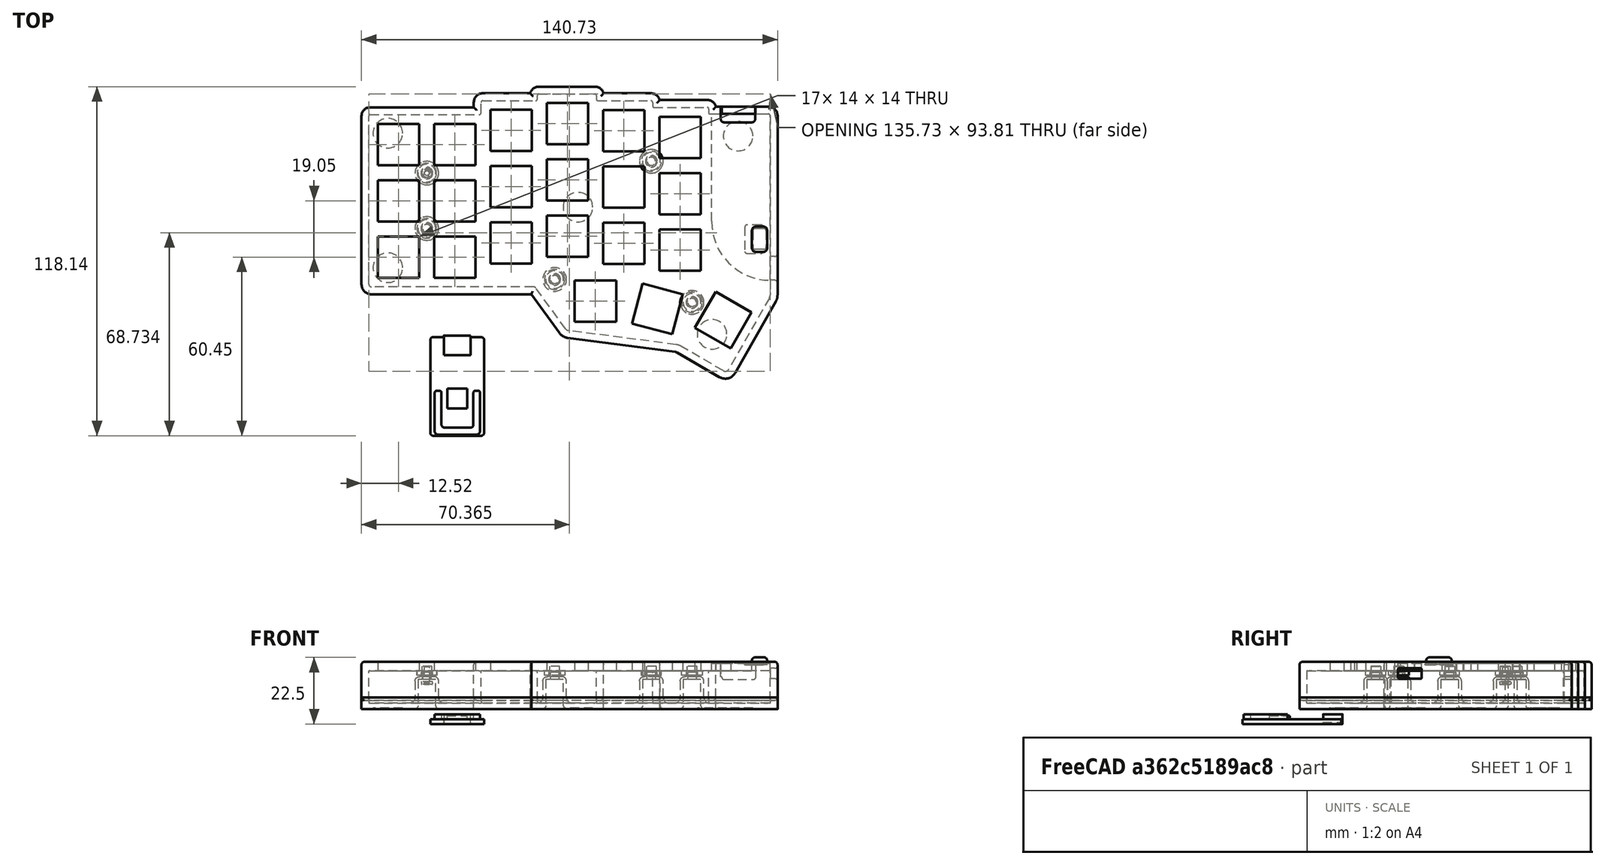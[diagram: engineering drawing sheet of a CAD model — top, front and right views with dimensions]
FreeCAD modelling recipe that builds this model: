
FCSTD DOCUMENT  (FreeCAD 1.0R39109 (Git))
Label: CaseV2
License: All rights reserved
LicenseURL: http://en.wikipedia.org/wiki/All_rights_reserved
objects: Sketcher::SketchObject×29, PartDesign::Pocket×15, PartDesign::Pad×13, PartDesign::Fillet×9, PartDesign::Body×5, Spreadsheet::Sheet×2
note: 174 computed .brp shape members not serialized (recipe doc carries the construction recipe); baked Part::Feature solids carry a one-line shape summary decoded from their .brp

FEATURE [Spreadsheet::Sheet] Spreadsheet
  cells = A1='PCBInnerBorderSpacing; B1(PCBInnerBorderSpacing)=1; A2='CaseTopBorderWitdh; B2(CaseTopBorderWitdh)=2; A3='SwitchBorderSpacing; B3(SwitchBorderSpacing)=2; A4='PCBBorderRadius; B4(PCBBorderRadius)=0.632; A5='PCBSmallStep; B5(PCBSmallStep)=2.25; A6='PCBBigStep; B6(PCBBigStep)=4.75; A7='SwitchplateHeight; B7(SwitchplateHeight)=2; A8='CaseTopTopBorderHeight; B8(CaseTopTopBorderHeight)=7; A9='CaseTopBottomBorderHeight; B9(CaseTopBottomBorderHeight)=6; A10='CaseColumnDiameter; B10(CaseColumnDiameter)=5; A11='ThreadedInsertHeight; B11(ThreadedInsertHeight)=3; A12='ThreadedInsertExtDiameter; B12(ThreadedInsertExtDiameter)=3.9; A13='PCBHoleSize; B13(PCBHoleSize)=4.2; A14='USBCPocketWidth; B14(USBCPocketWidth)=13.2; A15='USBCPocketHEIGHT; B15(USBCPocketHeight)=7.4; A16='CaseBottomPartHeight; B16(CaseBottomPartHeight)==CaseBottomFloorHeight + CaseBottomBorder; A17='CaseBottomFloorHeight; B17(CaseBottomFloorHeight)=3; A18='CaseBottomBorder; B18(CaseBottomBorder)=10; A19='ShadowLineWidth; B19(ShadowLineWidth)==CaseTopBorderWitdh - ShadowLineLipWidth; A20='ShadowLineLipWidth; B20(ShadowLineLipWidth)=0.6; A21='ResetSwitchHeight; B21(ResetSwitchHeight)=2.6; A22='PowerSwitchHeight; B22(PowerSwitchHeight)==3 - 1.4
FEATURE [Sketcher::SketchObject] Sketch108
  ArcFitTolerance = 0
  FullyConstrained = false
  MakeInternals = false
  Placement = pos=(0,0,8) rot=(0,0,1;0rad)
  sketch-geometry (26):
    g0: LineSegment StartX=-0.575516 StartY=59.75 StartZ=0 EndX=34.48 EndY=59.75 EndZ=0
    g1: LineSegment StartX=34.48 StartY=59.75 StartZ=0 EndX=34.48 EndY=61.4175 EndZ=0
    g2: ArcOfCircle CenterX=37.5625 CenterY=61.4175 CenterZ=0 NormalX=0 NormalY=0 NormalZ=1 AngleXU=0 Radius=3.08246 StartAngle=1.5708 EndAngle=3.14159
    g3: LineSegment StartX=37.5625 StartY=64.5 StartZ=0 EndX=53.5746 EndY=64.5 EndZ=0
    g4: ArcOfCircle CenterX=56.4769 CenterY=63.7531 CenterZ=0 NormalX=0 NormalY=0 NormalZ=1 AngleXU=0 Radius=2.99694 StartAngle=1.5708 EndAngle=2.8897
    g5: LineSegment StartX=56.4769 StartY=66.75 StartZ=0 EndX=75.4511 EndY=66.75 EndZ=0
    g6: ArcOfCircle CenterX=75.4511 CenterY=63.7211 CenterZ=0 NormalX=0 NormalY=0 NormalZ=1 AngleXU=0 Radius=3.0289 StartAngle=0.260077 EndAngle=1.5708
    g7: LineSegment StartX=78.3781 StartY=64.5 StartZ=0 EndX=94.3924 EndY=64.5 EndZ=0
    g8: ArcOfCircle CenterX=94.3924 CenterY=61.4124 CenterZ=0 NormalX=0 NormalY=0 NormalZ=1 AngleXU=0 Radius=3.08765 StartAngle=0.274732 EndAngle=1.5708
    g9: LineSegment StartX=97.3642 StartY=62.25 StartZ=0 EndX=113.447 EndY=62.25 EndZ=0
    g10: ArcOfCircle CenterX=113.447 CenterY=59.2166 CenterZ=0 NormalX=0 NormalY=0 NormalZ=1 AngleXU=0 Radius=3.03342 StartAngle=0.261223 EndAngle=1.5708
    g11: LineSegment StartX=116.377 StartY=60 StartZ=0 EndX=134.174 EndY=60 EndZ=0
    g12: ArcOfCircle CenterX=134.174 CenterY=56.9441 CenterZ=0 NormalX=0 NormalY=0 NormalZ=1 AngleXU=0 Radius=3.05595 StartAngle=0 EndAngle=1.5708
    g13: LineSegment StartX=137.23 StartY=56.9441 StartZ=0 EndX=137.23 EndY=-3.79962 EndZ=0
    g14: ArcOfCircle CenterX=132.762 CenterY=-3.79962 CenterZ=0 NormalX=0 NormalY=0 NormalZ=1 AngleXU=0 Radius=4.46789 StartAngle=5.76566 EndAngle=6.28319
    g15: LineSegment StartX=136.645 StartY=-6.01003 StartZ=0 EndX=122.927 EndY=-30.1062 EndZ=0
    g16: ArcOfCircle CenterX=119.558 CenterY=-28.1883 CenterZ=0 NormalX=0 NormalY=0 NormalZ=1 AngleXU=0 Radius=3.87659 StartAngle=4.18792 EndAngle=5.76566
    g17: LineSegment StartX=117.617 StartY=-31.5438 StartZ=0 EndX=103.226 EndY=-23.2181 EndZ=0
    g18: ArcOfCircle CenterX=102.379 CenterY=-24.6817 CenterZ=0 NormalX=0 NormalY=0 NormalZ=1 AngleXU=0 Radius=1.69085 StartAngle=1.04632 EndAngle=1.44147
    g19: LineSegment StartX=102.597 StartY=-23.0049 StartZ=0 EndX=66.2389 EndY=-18.2764 EndZ=0
    g20: ArcOfCircle CenterX=66.7544 CenterY=-14.3127 CenterZ=0 NormalX=0 NormalY=0 NormalZ=1 AngleXU=0 Radius=3.99704 StartAngle=3.77183 EndAngle=4.58306
    g21: LineSegment StartX=63.5253 StartY=-16.6683 StartZ=0 EndX=53.9192 EndY=-3.5 EndZ=0
    g22: LineSegment StartX=53.9192 StartY=-3.5 StartZ=0 EndX=-0.150389 EndY=-3.5 EndZ=0
    g23: ArcOfCircle CenterX=-0.150389 CenterY=-0.150389 CenterZ=0 NormalX=0 NormalY=0 NormalZ=1 AngleXU=0 Radius=3.34961 StartAngle=3.14159 EndAngle=4.71239
    g24: LineSegment StartX=-3.5 StartY=-0.150389 StartZ=0 EndX=-3.5 EndY=56.8255 EndZ=0
    g25: ArcOfCircle CenterX=-0.575516 CenterY=56.8255 CenterZ=0 NormalX=0 NormalY=0 NormalZ=1 AngleXU=0 Radius=2.92448 StartAngle=1.5708 EndAngle=3.14159
  constraints (36):
    c: Horizontal(g0)
    c: Coincident(g0,g1)
    c: Vertical(g1)
    c: Coincident(g1,g2)
    c: Coincident(g2,g3)
    c: Horizontal(g3)
    c: Coincident(g3,g4)
    c: Coincident(g4,g5)
    c: Horizontal(g5)
    c: Coincident(g5,g6)
    c: Coincident(g6,g7)
    c: Horizontal(g7)
    c: Coincident(g7,g8)
    c: Coincident(g8,g9)
    c: Horizontal(g9)
    c: Coincident(g9,g10)
    c: Coincident(g10,g11)
    c: Horizontal(g11)
    c: Coincident(g11,g12)
    c: Coincident(g12,g13)
    c: Vertical(g13)
    c: Coincident(g13,g14)
    c: Coincident(g14,g15)
    c: Coincident(g15,g16)
    c: Coincident(g16,g17)
    c: Coincident(g17,g18)
    c: Coincident(g18,g19)
    c: Coincident(g19,g20)
    c: Coincident(g20,g21)
    c: Coincident(g21,g22)
    c: Horizontal(g22)
    c: Coincident(g22,g23)
    c: Coincident(g23,g24)
    c: Vertical(g24)
    c: Coincident(g24,g25)
    c: Coincident(g25,g0)
FEATURE [PartDesign::Pad] Pad
  Direction = (0,0,1)
  Length = 4
  Length2 = 10
  Placement = pos=(0,0,8) rot=(0,0,1;0rad)
  Profile = -> Sketch108
  ReferenceAxis = -> Sketch108 [N_Axis]
  Suppressed = false
  Type = 0
FEATURE [Sketcher::SketchObject] Sketch110
  ArcFitTolerance = 0
  FullyConstrained = false
  MakeInternals = false
  Placement = pos=(0,0,8) rot=(0,0,1;0rad)
  sketch-geometry (26):
    g0: LineSegment StartX=-0.575516 StartY=59.75 StartZ=0 EndX=34.48 EndY=59.75 EndZ=0
    g1: LineSegment StartX=34.48 StartY=59.75 StartZ=0 EndX=34.48 EndY=61.4175 EndZ=0
    g2: ArcOfCircle CenterX=37.5625 CenterY=61.4175 CenterZ=0 NormalX=0 NormalY=0 NormalZ=1 AngleXU=0 Radius=3.08246 StartAngle=1.5708 EndAngle=3.14159
    g3: LineSegment StartX=37.5625 StartY=64.5 StartZ=0 EndX=53.5746 EndY=64.5 EndZ=0
    g4: ArcOfCircle CenterX=56.4769 CenterY=63.7531 CenterZ=0 NormalX=0 NormalY=0 NormalZ=1 AngleXU=0 Radius=2.99694 StartAngle=1.5708 EndAngle=2.8897
    g5: LineSegment StartX=56.4769 StartY=66.75 StartZ=0 EndX=75.4511 EndY=66.75 EndZ=0
    g6: ArcOfCircle CenterX=75.4511 CenterY=63.7211 CenterZ=0 NormalX=0 NormalY=0 NormalZ=1 AngleXU=0 Radius=3.0289 StartAngle=0.260077 EndAngle=1.5708
    g7: LineSegment StartX=78.3781 StartY=64.5 StartZ=0 EndX=94.3924 EndY=64.5 EndZ=0
    g8: ArcOfCircle CenterX=94.3924 CenterY=61.4124 CenterZ=0 NormalX=0 NormalY=0 NormalZ=1 AngleXU=0 Radius=3.08765 StartAngle=0.274732 EndAngle=1.5708
    g9: LineSegment StartX=97.3642 StartY=62.25 StartZ=0 EndX=113.447 EndY=62.25 EndZ=0
    g10: ArcOfCircle CenterX=113.447 CenterY=59.2166 CenterZ=0 NormalX=0 NormalY=0 NormalZ=1 AngleXU=0 Radius=3.03342 StartAngle=0.261223 EndAngle=1.5708
    g11: LineSegment StartX=116.377 StartY=60 StartZ=0 EndX=134.174 EndY=60 EndZ=0
    g12: ArcOfCircle CenterX=134.174 CenterY=56.9441 CenterZ=0 NormalX=0 NormalY=0 NormalZ=1 AngleXU=0 Radius=3.05595 StartAngle=0 EndAngle=1.5708
    g13: LineSegment StartX=137.23 StartY=56.9441 StartZ=0 EndX=137.23 EndY=-3.79962 EndZ=0
    g14: ArcOfCircle CenterX=132.762 CenterY=-3.79962 CenterZ=0 NormalX=0 NormalY=0 NormalZ=1 AngleXU=0 Radius=4.46789 StartAngle=5.76566 EndAngle=6.28319
    g15: LineSegment StartX=136.645 StartY=-6.01003 StartZ=0 EndX=122.927 EndY=-30.1062 EndZ=0
    g16: ArcOfCircle CenterX=119.558 CenterY=-28.1883 CenterZ=0 NormalX=0 NormalY=0 NormalZ=1 AngleXU=0 Radius=3.87659 StartAngle=4.18792 EndAngle=5.76566
    g17: LineSegment StartX=117.617 StartY=-31.5438 StartZ=0 EndX=103.226 EndY=-23.2181 EndZ=0
    g18: ArcOfCircle CenterX=102.379 CenterY=-24.6817 CenterZ=0 NormalX=0 NormalY=0 NormalZ=1 AngleXU=0 Radius=1.69085 StartAngle=1.04632 EndAngle=1.44147
    g19: LineSegment StartX=102.597 StartY=-23.0049 StartZ=0 EndX=66.2389 EndY=-18.2764 EndZ=0
    g20: ArcOfCircle CenterX=66.7544 CenterY=-14.3127 CenterZ=0 NormalX=0 NormalY=0 NormalZ=1 AngleXU=0 Radius=3.99704 StartAngle=3.77183 EndAngle=4.58306
    g21: LineSegment StartX=63.5253 StartY=-16.6683 StartZ=0 EndX=53.9192 EndY=-3.5 EndZ=0
    g22: LineSegment StartX=53.9192 StartY=-3.5 StartZ=0 EndX=-0.150389 EndY=-3.5 EndZ=0
    g23: ArcOfCircle CenterX=-0.150389 CenterY=-0.150389 CenterZ=0 NormalX=0 NormalY=0 NormalZ=1 AngleXU=0 Radius=3.34961 StartAngle=3.14159 EndAngle=4.71239
    g24: LineSegment StartX=-3.5 StartY=-0.150389 StartZ=0 EndX=-3.5 EndY=56.8255 EndZ=0
    g25: ArcOfCircle CenterX=-0.575516 CenterY=56.8255 CenterZ=0 NormalX=0 NormalY=0 NormalZ=1 AngleXU=0 Radius=2.92448 StartAngle=1.5708 EndAngle=3.14159
  constraints (36):
    c: Horizontal(g0)
    c: Coincident(g0,g1)
    c: Vertical(g1)
    c: Coincident(g1,g2)
    c: Coincident(g2,g3)
    c: Horizontal(g3)
    c: Coincident(g3,g4)
    c: Coincident(g4,g5)
    c: Horizontal(g5)
    c: Coincident(g5,g6)
    c: Coincident(g6,g7)
    c: Horizontal(g7)
    c: Coincident(g7,g8)
    c: Coincident(g8,g9)
    c: Horizontal(g9)
    c: Coincident(g9,g10)
    c: Coincident(g10,g11)
    c: Horizontal(g11)
    c: Coincident(g11,g12)
    c: Coincident(g12,g13)
    c: Vertical(g13)
    c: Coincident(g13,g14)
    c: Coincident(g14,g15)
    c: Coincident(g15,g16)
    c: Coincident(g16,g17)
    c: Coincident(g17,g18)
    c: Coincident(g18,g19)
    c: Coincident(g19,g20)
    c: Coincident(g20,g21)
    c: Coincident(g21,g22)
    c: Horizontal(g22)
    c: Coincident(g22,g23)
    c: Coincident(g23,g24)
    c: Vertical(g24)
    c: Coincident(g24,g25)
    c: Coincident(g25,g0)
FEATURE [PartDesign::Pad] Pad028  label="Main Shape"
  Direction = (0,0,1)
  Length = 13
  Length2 = 10
  Placement = pos=(0,0,8) rot=(0,0,1;0rad)
  Profile = -> Sketch110
  ReferenceAxis = -> Sketch110 [N_Axis]
  Suppressed = false
  Type = 0
FEATURE [Sketcher::SketchObject] Sketch109  label="Case.TopBorder001"
  ArcFitTolerance = 0
  AttachmentOffset = pos=(0,0,-13) rot=(0,0,1;0rad)
  AttachmentSupport = -> [Pad028]
  FullyConstrained = false
  MakeInternals = false
  MapMode = 5
  Placement = pos=(0,0,8) rot=(0,0,1;0rad)
  sketch-geometry (36):
    g0: LineSegment StartX=-0.575516 StartY=57.25 StartZ=0 EndX=36.2169 EndY=57.25 EndZ=0
    g1: LineSegment StartX=36.98 StartY=58.0131 StartZ=0 EndX=36.98 EndY=61.4175 EndZ=0
    g2: LineSegment StartX=37.5625 StartY=62 StartZ=0 EndX=55.4164 EndY=62 EndZ=0
    g3: LineSegment StartX=55.98 StartY=62.5636 StartZ=0 EndX=55.98 EndY=63.7531 EndZ=0
    g4: LineSegment StartX=56.4769 StartY=64.25 StartZ=0 EndX=75.4511 EndY=64.25 EndZ=0
    g5: LineSegment StartX=75.98 StartY=63.7211 StartZ=0 EndX=75.98 EndY=62.4917 EndZ=0
    g6: LineSegment StartX=76.4717 StartY=62 StartZ=0 EndX=94.3924 EndY=62 EndZ=0
    g7: LineSegment StartX=94.98 StartY=61.4124 StartZ=0 EndX=94.98 EndY=60.1933 EndZ=0
    g8: LineSegment StartX=95.4233 StartY=59.75 StartZ=0 EndX=113.447 EndY=59.75 EndZ=0
    g9: LineSegment StartX=113.98 StartY=59.2166 StartZ=0 EndX=113.98 EndY=57.754 EndZ=0
    g10: LineSegment StartX=114.234 StartY=57.5 StartZ=0 EndX=134.174 EndY=57.5 EndZ=0
    g11: LineSegment StartX=134.73 StartY=56.9441 StartZ=0 EndX=134.73 EndY=-3.79962 EndZ=0
    g12: LineSegment StartX=134.472 StartY=-4.7732 StartZ=0 EndX=120.755 EndY=-28.8693 EndZ=0
    g13: LineSegment StartX=118.869 StartY=-29.3799 StartZ=0 EndX=104.478 EndY=-21.0541 EndZ=0
    g14: LineSegment StartX=102.919 StartY=-20.5258 StartZ=0 EndX=66.5613 EndY=-15.7973 EndZ=0
    g15: LineSegment StartX=65.545 StartY=-15.195 StartZ=0 EndX=55.5069 EndY=-1.43443 EndZ=0
    g16: LineSegment StartX=54.6523 StartY=-1 StartZ=0 EndX=-0.150389 EndY=-1 EndZ=0
    g17: LineSegment StartX=-1 StartY=-0.150389 StartZ=0 EndX=-1 EndY=56.8255 EndZ=0
    g18: ArcOfCircle CenterX=37.5625 CenterY=61.4175 CenterZ=0 NormalX=0 NormalY=0 NormalZ=1 AngleXU=0 Radius=0.582459 StartAngle=1.5708 EndAngle=3.14159
    g19: ArcOfCircle CenterX=55.4164 CenterY=62.5636 CenterZ=0 NormalX=0 NormalY=0 NormalZ=1 AngleXU=0 Radius=0.563591 StartAngle=4.71239 EndAngle=6.28319
    g20: ArcOfCircle CenterX=56.4769 CenterY=63.7531 CenterZ=0 NormalX=0 NormalY=0 NormalZ=1 AngleXU=0 Radius=0.496936 StartAngle=1.5708 EndAngle=3.14159
    g21: ArcOfCircle CenterX=75.4511 CenterY=63.7211 CenterZ=0 NormalX=0 NormalY=0 NormalZ=1 AngleXU=0 Radius=0.528895 StartAngle=0 EndAngle=1.5708
    g22: ArcOfCircle CenterX=76.4717 CenterY=62.4917 CenterZ=0 NormalX=0 NormalY=0 NormalZ=1 AngleXU=0 Radius=0.491748 StartAngle=3.14159 EndAngle=4.71239
    g23: ArcOfCircle CenterX=94.3924 CenterY=61.4124 CenterZ=0 NormalX=0 NormalY=0 NormalZ=1 AngleXU=0 Radius=0.587645 StartAngle=0 EndAngle=1.5708
    g24: ArcOfCircle CenterX=95.4233 CenterY=60.1933 CenterZ=0 NormalX=0 NormalY=0 NormalZ=1 AngleXU=0 Radius=0.443253 StartAngle=3.14159 EndAngle=4.71239
    g25: ArcOfCircle CenterX=113.447 CenterY=59.2166 CenterZ=0 NormalX=0 NormalY=0 NormalZ=1 AngleXU=0 Radius=0.533416 StartAngle=0 EndAngle=1.5708
    g26: ArcOfCircle CenterX=134.174 CenterY=56.9441 CenterZ=0 NormalX=0 NormalY=0 NormalZ=1 AngleXU=0 Radius=0.555946 StartAngle=0 EndAngle=1.5708
    g27: ArcOfCircle CenterX=119.558 CenterY=-28.1883 CenterZ=0 NormalX=0 NormalY=0 NormalZ=1 AngleXU=0 Radius=1.37659 StartAngle=4.18792 EndAngle=5.76566
    g28: ArcOfCircle CenterX=-0.150389 CenterY=-0.150389 CenterZ=0 NormalX=0 NormalY=0 NormalZ=1 AngleXU=0 Radius=0.849611 StartAngle=3.14159 EndAngle=4.71239
    g29: ArcOfCircle CenterX=36.2169 CenterY=58.0131 CenterZ=0 NormalX=0 NormalY=0 NormalZ=1 AngleXU=0 Radius=0.763133 StartAngle=4.71239 EndAngle=6.28319
    g30: ArcOfCircle CenterX=114.234 CenterY=57.754 CenterZ=0 NormalX=0 NormalY=0 NormalZ=1 AngleXU=0 Radius=0.253983 StartAngle=3.14159 EndAngle=4.71239
    g31: ArcOfCircle CenterX=-0.575516 CenterY=56.8255 CenterZ=0 NormalX=0 NormalY=0 NormalZ=1 AngleXU=0 Radius=0.424484 StartAngle=1.5708 EndAngle=3.14159
    g32: ArcOfCircle CenterX=54.6523 CenterY=-2.05788 CenterZ=0 NormalX=0 NormalY=0 NormalZ=1 AngleXU=0 Radius=1.05788 StartAngle=0.630238 EndAngle=1.5708
    g33: ArcOfCircle CenterX=66.7544 CenterY=-14.3127 CenterZ=0 NormalX=0 NormalY=0 NormalZ=1 AngleXU=0 Radius=1.49704 StartAngle=3.77183 EndAngle=4.58306
    g34: ArcOfCircle CenterX=102.379 CenterY=-24.6817 CenterZ=0 NormalX=0 NormalY=0 NormalZ=1 AngleXU=0 Radius=4.19085 StartAngle=1.04632 EndAngle=1.44147
    g35: ArcOfCircle CenterX=132.762 CenterY=-3.79962 CenterZ=0 NormalX=0 NormalY=0 NormalZ=1 AngleXU=0 Radius=1.96789 StartAngle=5.76566 EndAngle=6.28319
  constraints (36):
    c: Coincident(g17,g28)
    c: Coincident(g16,g28)
    c: Coincident(g0,g29)
    c: Coincident(g1,g29)
    c: Coincident(g1,g18)
    c: Coincident(g2,g18)
    c: Coincident(g2,g19)
    c: Coincident(g3,g19)
    c: Coincident(g3,g20)
    c: Coincident(g4,g20)
    c: Coincident(g4,g21)
    c: Coincident(g5,g22)
    c: Coincident(g5,g21)
    c: Coincident(g6,g22)
    c: Coincident(g6,g23)
    c: Coincident(g7,g24)
    c: Coincident(g7,g23)
    c: Coincident(g8,g24)
    c: Coincident(g8,g25)
    c: Coincident(g9,g25)
    c: Coincident(g13,g27)
    c: Coincident(g12,g27)
    c: Coincident(g10,g26)
    c: Coincident(g11,g26)
    c: Tangent(g9,g30) = -1.5708
    c: Tangent(g10,g30) = -1.5708
    c: Tangent(g0,g31) = 1.5708
    c: Tangent(g17,g31) = 1.5708
    c: Tangent(g16,g32) = -1.5708
    c: Tangent(g15,g32) = -1.5708
    c: Tangent(g15,g33) = 1.5708
    c: Tangent(g14,g33) = 1.5708
    c: Tangent(g14,g34) = -1.5708
    c: Tangent(g13,g34) = -1.5708
    c: Tangent(g11,g35) = 1.5708
    c: Tangent(g12,g35) = 1.5708
FEATURE [PartDesign::Pocket] Pocket021  label="Border"
  BaseFeature = -> Pad028
  Direction = (0,0,-1)
  Length = 10
  Length2 = 5
  Placement = pos=(0,0,8) rot=(0,0,1;0rad)
  Profile = -> Sketch109
  ReferenceAxis = -> Sketch109 [N_Axis]
  Reversed = true
  Suppressed = false
  Type = 0
FEATURE [PartDesign::Fillet] Fillet003  label="Top Border Radius"
  Base = -> Pocket021 [Edge90,Edge91,Edge92,Edge89,Edge88,Edge87,Edge86,Edge85,Edge84,Edge83,Edge82,Edge81,Edge80,Edge79,Edge78,Edge77,Edge76,Edge75,Edge74,Edge73,Edge72,Edge71,Edge70,Edge10,Edge4,Edge7]
  BaseFeature = -> Pocket021
  Placement = pos=(0,0,8) rot=(0,0,1;0rad)
  Radius = 1
  SupportTransform = false
  Suppressed = false
  UseAllEdges = false
FEATURE [Sketcher::SketchObject] Sketch111  label="Case.SwitchPlatePocket001"
  ArcFitTolerance = 0
  AttachmentSupport = -> [Fillet003]
  FullyConstrained = false
  MakeInternals = false
  MapMode = 5
  Placement = pos=(0,0,21) rot=(0,0,1;0rad)
  expr: .Placement.Base.z = Spreadsheet001.CaseTopBottomBorderHeight + Spreadsheet001.SwitchplateHeight
  sketch-geometry (115):
    g0: LineSegment StartX=68.62 StartY=1.21 StartZ=0 EndX=82.62 EndY=1.21 EndZ=0
    g1: LineSegment StartX=82.62 StartY=1.21 StartZ=0 EndX=82.62 EndY=-12.79 EndZ=0
    g2: LineSegment StartX=82.62 StartY=-12.79 StartZ=0 EndX=68.62 EndY=-12.79 EndZ=0
    g3: LineSegment StartX=68.62 StartY=-12.79 StartZ=0 EndX=68.62 EndY=1.21 EndZ=0
    g4: LineSegment StartX=91.6293 StartY=0.0893034 StartZ=0 EndX=105.156 EndY=-3.52 EndZ=0
    g5: LineSegment StartX=105.156 StartY=-3.52 StartZ=0 EndX=101.547 EndY=-17.0467 EndZ=0
    g6: LineSegment StartX=101.547 StartY=-17.0467 StartZ=0 EndX=88.02 EndY=-13.4374 EndZ=0
    g7: LineSegment StartX=88.02 StartY=-13.4374 StartZ=0 EndX=91.6293 EndY=0.0893034 EndZ=0
    g8: LineSegment StartX=116.275 StartY=-2.66 StartZ=0 EndX=128.399 EndY=-9.66 EndZ=0
    g9: LineSegment StartX=128.399 StartY=-9.66 StartZ=0 EndX=121.399 EndY=-21.7844 EndZ=0
    g10: LineSegment StartX=121.399 StartY=-21.7844 StartZ=0 EndX=109.277 EndY=-14.7856 EndZ=0
    g11: LineSegment StartX=109.277 StartY=-14.7856 StartZ=0 EndX=116.275 EndY=-2.66 EndZ=0
    g12: Circle [constr] CenterX=108.346 CenterY=-6.24282 CenterZ=0 NormalX=0 NormalY=0 NormalZ=1 AngleXU=0 Radius=1.14051
    g13: Circle [constr] CenterX=61.8361 CenterY=1.51 CenterZ=0 NormalX=0 NormalY=0 NormalZ=1 AngleXU=0 Radius=1.14411
    g14: Circle [constr] CenterX=18.6 CenterY=18.76 CenterZ=0 NormalX=0 NormalY=0 NormalZ=1 AngleXU=0 Radius=1.14013
    g15: Circle [constr] CenterX=18.6 CenterY=37.51 CenterZ=0 NormalX=0 NormalY=0 NormalZ=1 AngleXU=0 Radius=1.14152
    g16: Circle [constr] CenterX=94.6 CenterY=41.2626 CenterZ=0 NormalX=0 NormalY=0 NormalZ=1 AngleXU=0 Radius=1.14274
    g17: LineSegment StartX=2.02 StartY=54.16 StartZ=0 EndX=2.02 EndY=40.16 EndZ=0
    g18: LineSegment StartX=2.02 StartY=2.06 StartZ=0 EndX=16.02 EndY=2.06 EndZ=0
    g19: LineSegment StartX=35.07 StartY=54.16 StartZ=0 EndX=21.07 EndY=54.16 EndZ=0
    g20: LineSegment StartX=35.07 StartY=40.16 StartZ=0 EndX=21.07 EndY=40.16 EndZ=0
    g21: LineSegment StartX=35.07 StartY=16.06 StartZ=0 EndX=21.07 EndY=16.06 EndZ=0
    g22: LineSegment StartX=2.02 StartY=35.11 StartZ=0 EndX=16.02 EndY=35.11 EndZ=0
    g23: LineSegment StartX=2.02 StartY=21.11 StartZ=0 EndX=16.02 EndY=21.11 EndZ=0
    g24: LineSegment StartX=16.02 StartY=54.16 StartZ=0 EndX=16.02 EndY=40.16 EndZ=0
    g25: LineSegment StartX=21.07 StartY=2.06 StartZ=0 EndX=21.07 EndY=16.06 EndZ=0
    g26: LineSegment StartX=35.07 StartY=54.16 StartZ=0 EndX=35.07 EndY=40.16 EndZ=0
    g27: LineSegment StartX=40.12 StartY=58.97 StartZ=0 EndX=40.12 EndY=44.97 EndZ=0
    g28: LineSegment StartX=54.12 StartY=6.87 StartZ=0 EndX=54.12 EndY=20.87 EndZ=0
    g29: LineSegment StartX=59.17 StartY=61.27 StartZ=0 EndX=59.17 EndY=47.27 EndZ=0
    g30: LineSegment StartX=73.17 StartY=9.17 StartZ=0 EndX=73.17 EndY=23.17 EndZ=0
    g31: LineSegment StartX=78.22 StartY=58.87 StartZ=0 EndX=78.22 EndY=44.87 EndZ=0
    g32: LineSegment StartX=92.22 StartY=6.77 StartZ=0 EndX=92.22 EndY=20.77 EndZ=0
    g33: LineSegment StartX=97.27 StartY=56.54 StartZ=0 EndX=97.27 EndY=42.54 EndZ=0
    g34: LineSegment StartX=111.27 StartY=56.54 StartZ=0 EndX=111.27 EndY=42.54 EndZ=0
    g35: LineSegment StartX=40.12 StartY=44.97 StartZ=0 EndX=54.12 EndY=44.97 EndZ=0
    g36: LineSegment StartX=40.12 StartY=39.92 StartZ=0 EndX=54.12 EndY=39.92 EndZ=0
    g37: LineSegment StartX=40.12 StartY=6.87 StartZ=0 EndX=54.12 EndY=6.87 EndZ=0
    g38: LineSegment StartX=59.17 StartY=9.17 StartZ=0 EndX=73.17 EndY=9.17 EndZ=0
    g39: LineSegment StartX=59.17 StartY=23.17 StartZ=0 EndX=73.17 EndY=23.17 EndZ=0
    g40: LineSegment StartX=59.17 StartY=28.22 StartZ=0 EndX=73.17 EndY=28.22 EndZ=0
    g41: LineSegment StartX=59.17 StartY=42.22 StartZ=0 EndX=73.17 EndY=42.22 EndZ=0
    g42: LineSegment StartX=59.17 StartY=47.27 StartZ=0 EndX=73.17 EndY=47.27 EndZ=0
    g43: LineSegment StartX=16.02 StartY=54.16 StartZ=0 EndX=2.02 EndY=54.16 EndZ=0
    g44: LineSegment StartX=16.02 StartY=40.16 StartZ=0 EndX=2.02 EndY=40.16 EndZ=0
    g45: LineSegment StartX=21.07 StartY=21.11 StartZ=0 EndX=35.07 EndY=21.11 EndZ=0
    g46: LineSegment StartX=16.02 StartY=16.06 StartZ=0 EndX=2.02 EndY=16.06 EndZ=0
    g47: LineSegment StartX=16.02 StartY=16.06 StartZ=0 EndX=16.02 EndY=2.06 EndZ=0
    g48: LineSegment StartX=21.07 StartY=21.11 StartZ=0 EndX=21.07 EndY=35.11 EndZ=0
    g49: LineSegment StartX=21.07 StartY=40.16 StartZ=0 EndX=21.07 EndY=54.16 EndZ=0
    g50: LineSegment StartX=16.02 StartY=35.11 StartZ=0 EndX=16.02 EndY=21.11 EndZ=0
    g51: LineSegment StartX=35.07 StartY=35.11 StartZ=0 EndX=35.07 EndY=21.11 EndZ=0
    g52: LineSegment StartX=35.07 StartY=16.06 StartZ=0 EndX=35.07 EndY=2.06 EndZ=0
    g53: LineSegment StartX=54.12 StartY=44.97 StartZ=0 EndX=54.12 EndY=58.97 EndZ=0
    g54: LineSegment StartX=54.12 StartY=25.92 StartZ=0 EndX=54.12 EndY=39.92 EndZ=0
    g55: LineSegment StartX=97.27 StartY=42.54 StartZ=0 EndX=111.27 EndY=42.54 EndZ=0
    g56: LineSegment StartX=97.27 StartY=37.49 StartZ=0 EndX=111.27 EndY=37.49 EndZ=0
    g57: LineSegment StartX=97.27 StartY=23.49 StartZ=0 EndX=111.27 EndY=23.49 EndZ=0
    g58: LineSegment StartX=97.27 StartY=18.44 StartZ=0 EndX=111.27 EndY=18.44 EndZ=0
    g59: LineSegment StartX=97.27 StartY=4.44 StartZ=0 EndX=111.27 EndY=4.44 EndZ=0
    g60: LineSegment StartX=73.17 StartY=28.22 StartZ=0 EndX=73.17 EndY=42.22 EndZ=0
    g61: LineSegment StartX=78.22 StartY=44.87 StartZ=0 EndX=92.22 EndY=44.87 EndZ=0
    g62: LineSegment StartX=73.17 StartY=47.27 StartZ=0 EndX=73.17 EndY=61.27 EndZ=0
    g63: LineSegment StartX=92.22 StartY=25.82 StartZ=0 EndX=92.22 EndY=39.82 EndZ=0
    g64: LineSegment StartX=78.22 StartY=6.77 StartZ=0 EndX=92.22 EndY=6.77 EndZ=0
    g65: LineSegment StartX=78.22 StartY=20.77 StartZ=0 EndX=92.22 EndY=20.77 EndZ=0
    g66: LineSegment StartX=78.22 StartY=25.82 StartZ=0 EndX=92.22 EndY=25.82 EndZ=0
    g67: LineSegment StartX=78.22 StartY=20.77 StartZ=0 EndX=78.22 EndY=6.77 EndZ=0
    g68: LineSegment StartX=78.22 StartY=39.82 StartZ=0 EndX=92.22 EndY=39.82 EndZ=0
    g69: LineSegment StartX=59.17 StartY=42.22 StartZ=0 EndX=59.17 EndY=28.22 EndZ=0
    g70: LineSegment StartX=78.22 StartY=39.82 StartZ=0 EndX=78.22 EndY=25.82 EndZ=0
    g71: LineSegment StartX=92.22 StartY=44.87 StartZ=0 EndX=92.22 EndY=58.87 EndZ=0
    g72: LineSegment StartX=40.12 StartY=39.92 StartZ=0 EndX=40.12 EndY=25.92 EndZ=0
    g73: LineSegment StartX=40.12 StartY=20.87 StartZ=0 EndX=40.12 EndY=6.87 EndZ=0
    g74: LineSegment StartX=97.27 StartY=18.44 StartZ=0 EndX=97.27 EndY=4.44 EndZ=0
    g75: LineSegment StartX=111.27 StartY=18.44 StartZ=0 EndX=111.27 EndY=4.44 EndZ=0
    g76: LineSegment StartX=111.27 StartY=37.49 StartZ=0 EndX=111.27 EndY=23.49 EndZ=0
    g77: LineSegment StartX=97.27 StartY=37.49 StartZ=0 EndX=97.27 EndY=23.49 EndZ=0
    g78: LineSegment StartX=78.22 StartY=58.87 StartZ=0 EndX=92.22 EndY=58.87 EndZ=0
    g79: LineSegment StartX=59.17 StartY=23.17 StartZ=0 EndX=59.17 EndY=9.17 EndZ=0
    g80: LineSegment StartX=2.02 StartY=35.11 StartZ=0 EndX=2.02 EndY=21.11 EndZ=0
    g81: LineSegment StartX=2.02 StartY=16.06 StartZ=0 EndX=2.02 EndY=2.06 EndZ=0
    g82: LineSegment StartX=111.27 StartY=56.54 StartZ=0 EndX=97.27 EndY=56.54 EndZ=0
    g83: LineSegment StartX=40.12 StartY=58.97 StartZ=0 EndX=54.12 EndY=58.97 EndZ=0
    g84: LineSegment StartX=40.12 StartY=20.87 StartZ=0 EndX=54.12 EndY=20.87 EndZ=0
    g85: LineSegment StartX=21.07 StartY=2.06 StartZ=0 EndX=35.07 EndY=2.06 EndZ=0
    g86: LineSegment StartX=40.12 StartY=25.92 StartZ=0 EndX=54.12 EndY=25.92 EndZ=0
    g87: LineSegment [constr] StartX=109.277 StartY=-14.7856 StartZ=0 EndX=109.277 EndY=-18.8356 EndZ=0
    g88: LineSegment [constr] StartX=88.02 StartY=-13.4374 StartZ=0 EndX=88.02 EndY=-63.3371 EndZ=0
    g89: LineSegment [constr] StartX=101.547 StartY=-17.0467 StartZ=0 EndX=109.277 EndY=-17.0467 EndZ=0
    g90: LineSegment [constr] StartX=0.08 StartY=56.27 StartZ=0 EndX=0.08 EndY=0.01 EndZ=0
    g91: LineSegment [constr] StartX=0.08 StartY=56.27 StartZ=0 EndX=38.09 EndY=56.27 EndZ=0
    g92: LineSegment [constr] StartX=0.08 StartY=0.01 StartZ=0 EndX=55.8461 EndY=0.01 EndZ=0
    g93: LineSegment [constr] StartX=55.8461 StartY=0.01 StartZ=0 EndX=66.6118 EndY=-14.7264 EndZ=0
    g94: LineSegment [constr] StartX=66.6118 StartY=-14.7264 StartZ=0 EndX=104.029 EndY=-19.5728 EndZ=0
    g95: LineSegment [constr] StartX=104.029 StartY=-19.5728 StartZ=0 EndX=119.75 EndY=-28.6236 EndZ=0
    g96: LineSegment [constr] StartX=119.75 StartY=-28.6236 StartZ=0 EndX=133.476 EndY=-4.78248 EndZ=0
    g97: LineSegment [constr] StartX=113.11 StartY=58.5126 StartZ=0 EndX=113.11 EndY=6.94265 EndZ=0
    g98: LineSegment [constr] StartX=113.11 StartY=6.94265 StartZ=0 EndX=133.476 EndY=-4.78248 EndZ=0
    g99: LineSegment [constr] StartX=94.09 StartY=58.5126 StartZ=0 EndX=113.11 EndY=58.5126 EndZ=0
    g100: LineSegment [constr] StartX=94.09 StartY=61.0126 StartZ=0 EndX=94.09 EndY=58.5126 EndZ=0
    g101: LineSegment [constr] StartX=38.09 StartY=61.02 StartZ=0 EndX=57.08 EndY=61.02 EndZ=0
    g102: LineSegment [constr] StartX=57.08 StartY=63.26 StartZ=0 EndX=75.08 EndY=63.26 EndZ=0
    g103: LineSegment [constr] StartX=57.08 StartY=63.26 StartZ=0 EndX=57.08 EndY=61.02 EndZ=0
    g104: LineSegment [constr] StartX=75.08 StartY=61.02 StartZ=0 EndX=75.08 EndY=63.26 EndZ=0
    g105: LineSegment [constr] StartX=75.08 StartY=61.02 StartZ=0 EndX=94.09 EndY=61.0126 EndZ=0
    g106: LineSegment [constr] StartX=38.09 StartY=61.02 StartZ=0 EndX=38.09 EndY=56.27 EndZ=0
    g107: LineSegment StartX=73.17 StartY=61.27 StartZ=0 EndX=59.17 EndY=61.27 EndZ=0
    g108: LineSegment StartX=21.07 StartY=35.11 StartZ=0 EndX=35.07 EndY=35.11 EndZ=0
    g109: LineSegment [constr] StartX=114.544 StartY=22.1265 StartZ=0 EndX=114.544 EndY=57.5 EndZ=0
    g110: LineSegment [constr] StartX=115.521 StartY=21.15 StartZ=0 EndX=134.73 EndY=21.15 EndZ=0
    g111: LineSegment [constr] StartX=114.544 StartY=57.5 StartZ=0 EndX=134.174 EndY=57.5 EndZ=0
    g112: LineSegment [constr] StartX=134.73 StartY=21.15 StartZ=0 EndX=134.73 EndY=56.9444 EndZ=0
    g113: ArcOfCircle [constr] CenterX=134.174 CenterY=56.9444 CenterZ=0 NormalX=0 NormalY=0 NormalZ=1 AngleXU=0 Radius=0.555602 StartAngle=0 EndAngle=1.5708
    g114: ArcOfCircle [constr] CenterX=115.521 CenterY=22.1265 CenterZ=0 NormalX=0 NormalY=0 NormalZ=1 AngleXU=0 Radius=0.976478 StartAngle=3.14159 EndAngle=4.71239
  constraints (97):
    c: Coincident(g18,g81)
    c: Coincident(g46,g81)
    c: Coincident(g23,g80)
    c: Coincident(g22,g80)
    c: Coincident(g17,g44)
    c: Coincident(g17,g43)
    c: Coincident(g18,g47)
    c: Coincident(g46,g47)
    c: Coincident(g23,g50)
    c: Coincident(g22,g50)
    c: Coincident(g24,g44)
    c: Coincident(g24,g43)
    c: Coincident(g25,g85)
    c: Coincident(g21,g25)
    c: Coincident(g45,g48)
    c: Coincident(g48,g108)
    c: Coincident(g20,g49)
    c: Coincident(g19,g49)
    c: Coincident(g52,g85)
    c: Coincident(g21,g52)
    c: Coincident(g45,g51)
    c: Coincident(g51,g108)
    c: Coincident(g20,g26)
    c: Coincident(g19,g26)
    c: Coincident(g37,g73)
    c: Coincident(g73,g84)
    c: Coincident(g72,g86)
    c: Coincident(g36,g72)
    c: Coincident(g27,g35)
    c: Coincident(g27,g83)
    c: Coincident(g28,g37)
    c: Coincident(g28,g84)
    c: Coincident(g54,g86)
    c: Coincident(g36,g54)
    c: Coincident(g35,g53)
    c: Coincident(g53,g83)
    c: Coincident(g38,g79)
    c: Coincident(g39,g79)
    c: Coincident(g40,g69)
    c: Coincident(g41,g69)
    c: Coincident(g29,g42)
    c: Coincident(g29,g107)
    c: Coincident(g2,g3)
    c: Coincident(g0,g3)
    c: Coincident(g30,g38)
    c: Coincident(g30,g39)
    c: Coincident(g40,g60)
    c: Coincident(g41,g60)
    c: Coincident(g42,g62)
    c: Coincident(g62,g107)
    c: Coincident(g64,g67)
    c: Coincident(g65,g67)
    c: Coincident(g66,g70)
    c: Coincident(g68,g70)
    c: Coincident(g31,g61)
    c: Coincident(g31,g78)
    c: Coincident(g1,g2)
    c: Coincident(g0,g1)
    c: Coincident(g6,g7)
    c: Coincident(g4,g7)
    c: Coincident(g32,g64)
    c: Coincident(g32,g65)
    c: Coincident(g63,g66)
    c: Coincident(g63,g68)
    c: Coincident(g61,g71)
    c: Coincident(g71,g78)
    c: Coincident(g59,g74)
    c: Coincident(g58,g74)
    c: Coincident(g57,g77)
    c: Coincident(g56,g77)
    c: Coincident(g33,g55)
    c: Coincident(g33,g82)
    c: Coincident(g5,g6)
    c: Coincident(g4,g5)
    c: Coincident(g10,g11)
    c: Coincident(g59,g75)
    c: Coincident(g58,g75)
    c: Coincident(g57,g76)
    c: Coincident(g56,g76)
    c: Coincident(g34,g55)
    c: Coincident(g34,g82)
    c: Coincident(g8,g11)
    c: Coincident(g9,g10)
    c: Coincident(g8,g9)
    c: Vertical(g109)
    c: Horizontal(g110)
    c: Coincident(g111,g109)
    c: Horizontal(g111)
    c: Coincident(g112,g110)
    c: Vertical(g112)
    c: Tangent(g111,g113) = 1.5708
    c: Tangent(g112,g113) = -1.5708
    c: Tangent(g109,g114) = 1.5708
    c: Tangent(g110,g114) = -1.5708
    c: Equal(g49,g19)
    c: Equal(g19,g26)
    c: Equal(g26,g20)
FEATURE [Spreadsheet::Sheet] Spreadsheet001
  cells = A1='PCBInnerBorderSpacing; B1(PCBInnerBorderSpacing)=1; A2='CaseTopBorderWitdh; B2(CaseTopBorderWitdh)=2; A3='SwitchBorderSpacing; B3(SwitchBorderSpacing)=2; A4='PCBBorderRadius; B4(PCBBorderRadius)=0.632; A5='PCBSmallStep; B5(PCBSmallStep)=2.25; A6='PCBBigStep; B6(PCBBigStep)=4.75; A7='SwitchplateHeight; B7(SwitchplateHeight)=2; A8='CaseTopTopBorderHeight; B8(CaseTopTopBorderHeight)=7; A9='CaseTopBottomBorderHeight; B9(CaseTopBottomBorderHeight)=6; A10='CaseColumnDiameter; B10(CaseColumnDiameter)=5; A11='ThreadedInsertHeight; B11(ThreadedInsertHeight)=3; A12='ThreadedInsertExtDiameter; B12(ThreadedInsertExtDiameter)=3.9; A13='PCBHoleSize; B13(PCBHoleSize)=4.2; A14='USBCPocketWidth; B14(USBCPocketWidth)=13.2; A15='USBCPocketHEIGHT; B15(USBCPocketHeight)=7.4; A16='CaseBottomPartHeight; B16(CaseBottomPartHeight)==CaseBottomFloorHeight + CaseBottomBorder; A17='CaseBottomFloorHeight; B17(CaseBottomFloorHeight)=3; A18='CaseBottomBorder; B18(CaseBottomBorder)=10; A19='ShadowLineWidth; B19(ShadowLineWidth)==CaseTopBorderWitdh - ShadowLineLipWidth; A20='ShadowLineLipWidth; B20(ShadowLineLipWidth)=0.6; A21='ResetSwitchHeight; B21(ResetSwitchHeight)=2.6; A22='PowerSwitchHeight; B22(PowerSwitchHeight)==3 - 1.4
FEATURE [PartDesign::Pocket] Pocket022  label="Switch Plate"
  BaseFeature = -> Fillet003
  Direction = (0,0,-1)
  Length = 3
  Length2 = 5
  Placement = pos=(0,0,8) rot=(0,0,1;0rad)
  Profile = -> Sketch111
  ReferenceAxis = -> Sketch111 [N_Axis]
  Suppressed = false
  Type = 0
FEATURE [Sketcher::SketchObject] Sketch114
  ArcFitTolerance = 0
  AttachmentSupport = -> [Pocket022]
  FullyConstrained = false
  MakeInternals = false
  MapMode = 5
  Placement = pos=(137.23,0,8) rot=(0.57735,0.57735,0.57735;2.0944rad)
  sketch-geometry (10):
    g0: LineSegment StartX=1.24469 StartY=10.4386 StartZ=0 EndX=1.24469 EndY=7.69946 EndZ=0
    g1: LineSegment StartX=1.64469 StartY=10.8386 StartZ=0 EndX=8.89469 EndY=10.8386 EndZ=0
    g2: LineSegment StartX=1.64469 StartY=7.29946 StartZ=0 EndX=8.89469 EndY=7.29946 EndZ=0
    g3: LineSegment StartX=9.29469 StartY=10.4386 StartZ=0 EndX=9.29469 EndY=7.69946 EndZ=0
    g4: ArcOfCircle CenterX=1.64469 CenterY=10.4386 CenterZ=0 NormalX=0 NormalY=0 NormalZ=1 AngleXU=0 Radius=0.4 StartAngle=1.5708 EndAngle=3.14159
    g5: ArcOfCircle CenterX=1.64469 CenterY=7.69946 CenterZ=0 NormalX=0 NormalY=0 NormalZ=1 AngleXU=0 Radius=0.4 StartAngle=3.14159 EndAngle=4.71239
    g6: ArcOfCircle CenterX=8.89469 CenterY=7.69946 CenterZ=0 NormalX=0 NormalY=0 NormalZ=1 AngleXU=0 Radius=0.4 StartAngle=4.71239 EndAngle=6.28319
    g7: ArcOfCircle CenterX=8.89469 CenterY=10.4386 CenterZ=0 NormalX=0 NormalY=0 NormalZ=1 AngleXU=0 Radius=0.4 StartAngle=0 EndAngle=1.5708
    g8: LineSegment [constr] StartX=1.24469 StartY=10.4386 StartZ=0 EndX=9.29469 EndY=10.4386 EndZ=0
    g9: LineSegment [constr] StartX=8.89469 StartY=10.8386 StartZ=0 EndX=8.89469 EndY=7.29946 EndZ=0
  constraints (21):
    c: Horizontal(g1)
    c: Horizontal(g2)
    c: Vertical(g3)
    c: Tangent(g1,g4) = 1.5708
    c: Tangent(g0,g4) = -1.5708
    c: Tangent(g0,g5) = -1.5708
    c: Tangent(g2,g5) = -1.5708
    c: Tangent(g3,g6) = 1.5708
    c: Tangent(g2,g6) = -1.5708
    c: Tangent(g1,g7) = 1.5708
    c: Tangent(g3,g7) = 1.5708
    c: Radius(g7) = 0.4
    c: Radius(g4) = 0.4
    c: Radius(g5) = 0.4
    c: Radius(g6) = 0.4
    c: Coincident(g8,g0)
    c: Coincident(g8,g3)
    c: Horizontal(g8)
    c: Distance(g8) = 8.05
    c: Coincident(g9,g1)
    c: Coincident(g9,g2)
FEATURE [PartDesign::Pocket] Pocket023  label="OnOff Switch"
  BaseFeature = -> Pocket022
  Direction = (-1,0,0)
  Length = 2.5
  Length2 = 5
  Placement = pos=(0,0,8) rot=(0,0,1;0rad)
  Profile = -> Sketch114
  ReferenceAxis = -> Sketch114 [N_Axis]
  Suppressed = false
  Type = 0
FEATURE [Sketcher::SketchObject] Sketch115
  ArcFitTolerance = 0
  AttachmentSupport = -> [Pocket023]
  ExternalGeometry = -> [Sketch109]
  FullyConstrained = false
  MakeInternals = false
  MapMode = 5
  Placement = pos=(0,0,18) rot=(1,0,0;3.14159rad)
  sketch-geometry (6):
    g0: ArcOfCircle CenterX=134.174 CenterY=-56.9441 CenterZ=0 NormalX=0 NormalY=0 NormalZ=1 AngleXU=0 Radius=0.555946 StartAngle=4.71239 EndAngle=6.28319
    g1: LineSegment [constr] StartX=134.73 StartY=-21.2447 StartZ=0 EndX=114.919 EndY=-21.2447 EndZ=0
    g2: LineSegment StartX=114.919 StartY=-21.2447 StartZ=0 EndX=114.919 EndY=-57.5 EndZ=0
    g3: LineSegment StartX=114.919 StartY=-57.5 StartZ=0 EndX=134.174 EndY=-57.5 EndZ=0
    g4: LineSegment StartX=134.73 StartY=-1.22951 StartZ=0 EndX=134.73 EndY=-56.9441 EndZ=0
    g5: ArcOfCircle CenterX=134.9 CenterY=-21.2101 CenterZ=0 NormalX=0 NormalY=0 NormalZ=1 AngleXU=0 Radius=19.9813 StartAngle=1.57933 EndAngle=3.14332
  constraints (13):
    c: Coincident(g0,g-4)
    c: Coincident(g0,g-5)
    c: PointOnObject(g1,g-4)
    c: Horizontal(g1)
    c: Coincident(g2,g1)
    c: PointOnObject(g2,g-5)
    c: Vertical(g2)
    c: Coincident(g3,g2)
    c: Coincident(g3,g0)
    c: PointOnObject(g4,g-4)
    c: Coincident(g4,g0)
    c: Coincident(g5,g4)
    c: Coincident(g5,g2)
FEATURE [PartDesign::Pocket] Pocket024  label="Microcontroler Space"
  BaseFeature = -> Pocket023
  Direction = (0,0,1)
  Length = 2.5
  Length2 = 5
  Placement = pos=(0,0,8) rot=(0,0,1;0rad)
  Profile = -> Sketch115
  ReferenceAxis = -> Sketch115 [N_Axis]
  Suppressed = false
  Type = 0
FEATURE [Sketcher::SketchObject] Sketch116
  ArcFitTolerance = 0
  AttachmentSupport = -> [Pocket024]
  ExternalGeometry = -> [Pocket024]
  FullyConstrained = false
  MakeInternals = false
  MapMode = 5
  Placement = pos=(0,60,8) rot=(0,0.707107,0.707107;3.14159rad)
  sketch-geometry (13):
    g0: LineSegment [constr] StartX=-134.73 StartY=5 StartZ=0 EndX=-133.114 EndY=5 EndZ=0
    g1: LineSegment StartX=-129.965 StartY=12.0454 StartZ=0 EndX=-119.17 EndY=12.0454 EndZ=0
    g2: ArcOfCircle CenterX=-119.17 CenterY=11.2402 CenterZ=0 NormalX=0 NormalY=0 NormalZ=1 AngleXU=0 Radius=0.805245 StartAngle=-9e-16 EndAngle=1.5708
    g3: LineSegment StartX=-118.365 StartY=11.2402 StartZ=0 EndX=-118.365 EndY=7.85065 EndZ=0
    g4: ArcOfCircle CenterX=-119.17 CenterY=7.85065 CenterZ=0 NormalX=0 NormalY=0 NormalZ=1 AngleXU=0 Radius=0.805245 StartAngle=4.71239 EndAngle=6.28319
    g5: LineSegment StartX=-119.17 StartY=7.0454 StartZ=0 EndX=-128.965 EndY=7.0454 EndZ=0
    g6: GeomPoint [constr] X=-133.114 Y=7.0454 Z=0
    g7: GeomPoint [constr] X=-118.365 Y=12.0454 Z=0
    g8: LineSegment [constr] StartX=-133.114 StartY=6.26145 StartZ=0 EndX=-118.365 EndY=6.26145 EndZ=0
    g9: LineSegment [constr] StartX=-122.72 StartY=12.0454 StartZ=0 EndX=-122.72 EndY=7.0454 EndZ=0
    g10: LineSegment [constr] StartX=-118.365 StartY=9.74283 StartZ=0 EndX=-129.965 EndY=9.74283 EndZ=0
    g11: LineSegment StartX=-129.965 StartY=8.0454 StartZ=0 EndX=-129.965 EndY=12.0454 EndZ=0
    g12: ArcOfCircle CenterX=-128.965 CenterY=8.0454 CenterZ=0 NormalX=0 NormalY=0 NormalZ=1 AngleXU=0 Radius=1 StartAngle=3.14159 EndAngle=4.71239
  constraints (27):
    c: Horizontal(g0)
    c: Tangent(g1,g2) = 1.5708
    c: Tangent(g2,g3) = 1.5708
    c: Tangent(g3,g4) = 1.5708
    c: Tangent(g4,g5) = 1.5708
    c: Horizontal(g1)
    c: Horizontal(g5)
    c: Vertical(g3)
    c: Equal(g2,g4)
    c: PointOnObject(g6,g5)
    c: PointOnObject(g7,g1)
    c: PointOnObject(g7,g3)
    c: PointOnObject(g8,g3)
    c: Horizontal(g8)
    c: PointOnObject(g9,g1)
    c: PointOnObject(g9,g5)
    c: Vertical(g9)
    c: Distance(g9) = 5
    c: PointOnObject(g10,g3)
    c: Horizontal(g10)
    c: Distance(g10) = 11.6
    c: Vertical(g11)
    c: PointOnObject(g10,g11)
    c: Coincident(g1,g11)
    c: Tangent(g5,g12) = 1.5708
    c: Tangent(g11,g12) = 1.5708
    c: Radius(g12) = 1
FEATURE [PartDesign::Pocket] Pocket025  label="USBC Hole"
  BaseFeature = -> Pocket024
  Direction = (0,-1,2e-16)
  Length = 5
  Length2 = 5
  Placement = pos=(0,0,8) rot=(0,0,1;0rad)
  Profile = -> Sketch116
  ReferenceAxis = -> Sketch116 [N_Axis]
  Suppressed = false
  Type = 0
FEATURE [Sketcher::SketchObject] Sketch
  ArcFitTolerance = 0
  AttachmentSupport = -> [Pocket025]
  FullyConstrained = false
  MakeInternals = false
  MapMode = 5
  Placement = pos=(0,0,21) rot=(0,0,1;0rad)
  sketch-geometry (23):
    g0: ArcOfCircle [constr] CenterX=132.868 CenterY=11.7057 CenterZ=0 NormalX=0 NormalY=0 NormalZ=1 AngleXU=0 Radius=1.50044 StartAngle=4.71239 EndAngle=6.28319
    g1: LineSegment [constr] StartX=132.868 StartY=10.2053 StartZ=0 EndX=129.369 EndY=10.2053 EndZ=0
    g2: ArcOfCircle [constr] CenterX=129.369 CenterY=11.7057 CenterZ=0 NormalX=0 NormalY=0 NormalZ=1 AngleXU=0 Radius=1.50044 StartAngle=3.14159 EndAngle=4.71239
    g3: LineSegment [constr] StartX=127.868 StartY=11.7057 StartZ=0 EndX=127.868 EndY=18.7049 EndZ=0
    g4: ArcOfCircle [constr] CenterX=129.369 CenterY=18.7049 CenterZ=0 NormalX=0 NormalY=0 NormalZ=1 AngleXU=0 Radius=1.50044 StartAngle=1.5708 EndAngle=3.14159
    g5: LineSegment [constr] StartX=129.369 StartY=20.2053 StartZ=0 EndX=132.868 EndY=20.2053 EndZ=0
    g6: ArcOfCircle [constr] CenterX=132.868 CenterY=18.7049 CenterZ=0 NormalX=0 NormalY=0 NormalZ=1 AngleXU=0 Radius=1.50044 StartAngle=-9e-16 EndAngle=1.5708
    g7: LineSegment [constr] StartX=134.368 StartY=18.7049 StartZ=0 EndX=134.368 EndY=11.7057 EndZ=0
    g8: GeomPoint [constr] X=134.368 Y=10.2053 Z=0
    g9: GeomPoint [constr] X=127.868 Y=20.2053 Z=0
    g10: LineSegment [constr] StartX=134.368 StartY=15.857 StartZ=0 EndX=133.368 EndY=15.857 EndZ=0
    g11: LineSegment [constr] StartX=127.868 StartY=15.2088 StartZ=0 EndX=128.868 EndY=15.2088 EndZ=0
    g12: LineSegment [constr] StartX=131.125 StartY=20.2053 StartZ=0 EndX=131.125 EndY=18.7053 EndZ=0
    g13: LineSegment [constr] StartX=130.851 StartY=10.2053 StartZ=0 EndX=130.851 EndY=11.7053 EndZ=0
    g14: LineSegment StartX=132.568 StartY=18.7053 StartZ=0 EndX=129.668 EndY=18.7053 EndZ=0
    g15: LineSegment StartX=132.568 StartY=11.7053 StartZ=0 EndX=129.668 EndY=11.7053 EndZ=0
    g16: LineSegment StartX=133.368 StartY=17.9053 StartZ=0 EndX=133.368 EndY=12.5053 EndZ=0
    g17: LineSegment StartX=128.868 StartY=17.9053 StartZ=0 EndX=128.868 EndY=12.5053 EndZ=0
    g18: ArcOfCircle CenterX=129.668 CenterY=17.9053 CenterZ=0 NormalX=0 NormalY=0 NormalZ=1 AngleXU=0 Radius=0.8 StartAngle=1.5708 EndAngle=3.14159
    g19: ArcOfCircle CenterX=132.568 CenterY=17.9053 CenterZ=0 NormalX=0 NormalY=0 NormalZ=1 AngleXU=0 Radius=0.8 StartAngle=-9e-16 EndAngle=1.5708
    g20: ArcOfCircle CenterX=132.568 CenterY=12.5053 CenterZ=0 NormalX=0 NormalY=0 NormalZ=1 AngleXU=0 Radius=0.8 StartAngle=4.71239 EndAngle=6.28319
    g21: ArcOfCircle CenterX=129.668 CenterY=12.5053 CenterZ=0 NormalX=0 NormalY=0 NormalZ=1 AngleXU=0 Radius=0.8 StartAngle=3.14159 EndAngle=4.71239
    g22: LineSegment [constr] StartX=130.678 StartY=18.7053 StartZ=0 EndX=130.678 EndY=11.7053 EndZ=0
  constraints (55):
    c: Tangent(g0,g1) = 1.5708
    c: Tangent(g1,g2) = 1.5708
    c: Tangent(g2,g3) = 1.5708
    c: Tangent(g3,g4) = 1.5708
    c: Tangent(g4,g5) = 1.5708
    c: Tangent(g5,g6) = 1.5708
    c: Tangent(g6,g7) = 1.5708
    c: Tangent(g7,g0) = 1.5708
    c: Horizontal(g1)
    c: Horizontal(g5)
    c: Vertical(g3)
    c: Vertical(g7)
    c: Equal(g0,g2)
    c: Equal(g2,g4)
    c: Equal(g4,g6)
    c: PointOnObject(g8,g1)
    c: PointOnObject(g8,g7)
    c: PointOnObject(g9,g3)
    c: PointOnObject(g9,g5)
    c: PointOnObject(g10,g7)
    c: Horizontal(g10)
    c: PointOnObject(g11,g3)
    c: Horizontal(g11)
    c: Distance(g11) = 1
    c: Distance(g10) = 1
    c: PointOnObject(g12,g5)
    c: Vertical(g12)
    c: PointOnObject(g13,g1)
    c: Vertical(g13)
    c: Distance(g12) = 1.5
    c: Distance(g13) = 1.5
    c: Horizontal(g14)
    c: Horizontal(g15)
    c: Vertical(g16)
    c: Vertical(g17)
    c: Tangent(g14,g18) = -1.5708
    c: Tangent(g17,g18) = -1.5708
    c: Tangent(g14,g19) = -1.5708
    c: Tangent(g16,g19) = 1.5708
    c: Tangent(g16,g20) = 1.5708
    c: Tangent(g15,g20) = 1.5708
    c: Tangent(g17,g21) = -1.5708
    c: Tangent(g15,g21) = 1.5708
    c: Radius(g19) = 0.8
    c: Radius(g21) = 0.8
    c: Radius(g20) = 0.8
    c: Radius(g18) = 0.8
    c: PointOnObject(g11,g17)
    c: PointOnObject(g10,g16)
    c: PointOnObject(g22,g14)
    c: PointOnObject(g22,g15)
    c: Vertical(g22)
    c: Distance(g22) = 7
    c: PointOnObject(g12,g14)
    c: PointOnObject(g13,g15)
FEATURE [PartDesign::Pocket] Pocket026  label="Reset Button"
  BaseFeature = -> Pocket025
  Direction = (0,0,-1)
  Length = 5
  Length2 = 5
  Placement = pos=(0,0,8) rot=(0,0,1;0rad)
  Profile = -> Sketch
  ReferenceAxis = -> Sketch [N_Axis]
  Suppressed = false
  Type = 0
FEATURE [PartDesign::Fillet] Fillet  label="Bottom Border Radius"
  Base = -> Pocket026 [Edge22,Edge24,Edge26,Edge28,Edge30,Edge32,Edge34,Edge33,Edge31,Edge29,Edge27,Edge25,Edge23,Edge21,Edge19,Edge17,Edge15,Edge13,Edge11,Edge3,Edge6,Edge12,Edge14,Edge16,Edge18,Edge20]
  BaseFeature = -> Pocket026
  Placement = pos=(0,0,8) rot=(0,0,1;0rad)
  Radius = 1
  SupportTransform = false
  Suppressed = false
  UseAllEdges = false
FEATURE [Sketcher::SketchObject] Sketch058  label="Case.TopBorder"
  ArcFitTolerance = 0
  AttachmentSupport = -> [Pad]
  FullyConstrained = false
  MakeInternals = false
  MapMode = 5
  Placement = pos=(0,0,12) rot=(0,0,1;0rad)
  sketch-geometry (36):
    g0: LineSegment StartX=-0.575516 StartY=57.25 StartZ=0 EndX=36.2169 EndY=57.25 EndZ=0
    g1: LineSegment StartX=36.98 StartY=58.0131 StartZ=0 EndX=36.98 EndY=61.4175 EndZ=0
    g2: LineSegment StartX=37.5625 StartY=62 StartZ=0 EndX=55.4164 EndY=62 EndZ=0
    g3: LineSegment StartX=55.98 StartY=62.5636 StartZ=0 EndX=55.98 EndY=63.7531 EndZ=0
    g4: LineSegment StartX=56.4769 StartY=64.25 StartZ=0 EndX=75.4511 EndY=64.25 EndZ=0
    g5: LineSegment StartX=75.98 StartY=63.7211 StartZ=0 EndX=75.98 EndY=62.4917 EndZ=0
    g6: LineSegment StartX=76.4717 StartY=62 StartZ=0 EndX=94.3924 EndY=62 EndZ=0
    g7: LineSegment StartX=94.98 StartY=61.4124 StartZ=0 EndX=94.98 EndY=60.1933 EndZ=0
    g8: LineSegment StartX=95.4233 StartY=59.75 StartZ=0 EndX=113.447 EndY=59.75 EndZ=0
    g9: LineSegment StartX=113.98 StartY=59.2166 StartZ=0 EndX=113.98 EndY=57.754 EndZ=0
    g10: LineSegment StartX=114.234 StartY=57.5 StartZ=0 EndX=134.174 EndY=57.5 EndZ=0
    g11: LineSegment StartX=134.73 StartY=56.9441 StartZ=0 EndX=134.73 EndY=-3.79962 EndZ=0
    g12: LineSegment StartX=134.472 StartY=-4.7732 StartZ=0 EndX=120.755 EndY=-28.8693 EndZ=0
    g13: LineSegment StartX=118.869 StartY=-29.3799 StartZ=0 EndX=104.478 EndY=-21.0541 EndZ=0
    g14: LineSegment StartX=102.919 StartY=-20.5258 StartZ=0 EndX=66.5613 EndY=-15.7973 EndZ=0
    g15: LineSegment StartX=65.545 StartY=-15.195 StartZ=0 EndX=55.5069 EndY=-1.43443 EndZ=0
    g16: LineSegment StartX=54.6523 StartY=-1 StartZ=0 EndX=-0.150389 EndY=-1 EndZ=0
    g17: LineSegment StartX=-1 StartY=-0.150389 StartZ=0 EndX=-1 EndY=56.8255 EndZ=0
    g18: ArcOfCircle CenterX=37.5625 CenterY=61.4175 CenterZ=0 NormalX=0 NormalY=0 NormalZ=1 AngleXU=0 Radius=0.582459 StartAngle=1.5708 EndAngle=3.14159
    g19: ArcOfCircle CenterX=55.4164 CenterY=62.5636 CenterZ=0 NormalX=0 NormalY=0 NormalZ=1 AngleXU=0 Radius=0.563591 StartAngle=4.71239 EndAngle=6.28319
    g20: ArcOfCircle CenterX=56.4769 CenterY=63.7531 CenterZ=0 NormalX=0 NormalY=0 NormalZ=1 AngleXU=0 Radius=0.496936 StartAngle=1.5708 EndAngle=3.14159
    g21: ArcOfCircle CenterX=75.4511 CenterY=63.7211 CenterZ=0 NormalX=0 NormalY=0 NormalZ=1 AngleXU=0 Radius=0.528895 StartAngle=0 EndAngle=1.5708
    g22: ArcOfCircle CenterX=76.4717 CenterY=62.4917 CenterZ=0 NormalX=0 NormalY=0 NormalZ=1 AngleXU=0 Radius=0.491748 StartAngle=3.14159 EndAngle=4.71239
    g23: ArcOfCircle CenterX=94.3924 CenterY=61.4124 CenterZ=0 NormalX=0 NormalY=0 NormalZ=1 AngleXU=0 Radius=0.587645 StartAngle=0 EndAngle=1.5708
    g24: ArcOfCircle CenterX=95.4233 CenterY=60.1933 CenterZ=0 NormalX=0 NormalY=0 NormalZ=1 AngleXU=0 Radius=0.443253 StartAngle=3.14159 EndAngle=4.71239
    g25: ArcOfCircle CenterX=113.447 CenterY=59.2166 CenterZ=0 NormalX=0 NormalY=0 NormalZ=1 AngleXU=0 Radius=0.533416 StartAngle=0 EndAngle=1.5708
    g26: ArcOfCircle CenterX=134.174 CenterY=56.9441 CenterZ=0 NormalX=0 NormalY=0 NormalZ=1 AngleXU=0 Radius=0.555946 StartAngle=0 EndAngle=1.5708
    g27: ArcOfCircle CenterX=119.558 CenterY=-28.1883 CenterZ=0 NormalX=0 NormalY=0 NormalZ=1 AngleXU=0 Radius=1.37659 StartAngle=4.18792 EndAngle=5.76566
    g28: ArcOfCircle CenterX=-0.150389 CenterY=-0.150389 CenterZ=0 NormalX=0 NormalY=0 NormalZ=1 AngleXU=0 Radius=0.849611 StartAngle=3.14159 EndAngle=4.71239
    g29: ArcOfCircle CenterX=36.2169 CenterY=58.0131 CenterZ=0 NormalX=0 NormalY=0 NormalZ=1 AngleXU=0 Radius=0.763133 StartAngle=4.71239 EndAngle=6.28319
    g30: ArcOfCircle CenterX=114.234 CenterY=57.754 CenterZ=0 NormalX=0 NormalY=0 NormalZ=1 AngleXU=0 Radius=0.253983 StartAngle=3.14159 EndAngle=4.71239
    g31: ArcOfCircle CenterX=-0.575516 CenterY=56.8255 CenterZ=0 NormalX=0 NormalY=0 NormalZ=1 AngleXU=0 Radius=0.424484 StartAngle=1.5708 EndAngle=3.14159
    g32: ArcOfCircle CenterX=54.6523 CenterY=-2.05788 CenterZ=0 NormalX=0 NormalY=0 NormalZ=1 AngleXU=0 Radius=1.05788 StartAngle=0.630238 EndAngle=1.5708
    g33: ArcOfCircle CenterX=66.7544 CenterY=-14.3127 CenterZ=0 NormalX=0 NormalY=0 NormalZ=1 AngleXU=0 Radius=1.49704 StartAngle=3.77183 EndAngle=4.58306
    g34: ArcOfCircle CenterX=102.379 CenterY=-24.6817 CenterZ=0 NormalX=0 NormalY=0 NormalZ=1 AngleXU=0 Radius=4.19085 StartAngle=1.04632 EndAngle=1.44147
    g35: ArcOfCircle CenterX=132.762 CenterY=-3.79962 CenterZ=0 NormalX=0 NormalY=0 NormalZ=1 AngleXU=0 Radius=1.96789 StartAngle=5.76566 EndAngle=6.28319
  constraints (36):
    c: Coincident(g17,g28)
    c: Coincident(g16,g28)
    c: Coincident(g0,g29)
    c: Coincident(g1,g29)
    c: Coincident(g1,g18)
    c: Coincident(g2,g18)
    c: Coincident(g2,g19)
    c: Coincident(g3,g19)
    c: Coincident(g3,g20)
    c: Coincident(g4,g20)
    c: Coincident(g4,g21)
    c: Coincident(g5,g22)
    c: Coincident(g5,g21)
    c: Coincident(g6,g22)
    c: Coincident(g6,g23)
    c: Coincident(g7,g24)
    c: Coincident(g7,g23)
    c: Coincident(g8,g24)
    c: Coincident(g8,g25)
    c: Coincident(g9,g25)
    c: Coincident(g13,g27)
    c: Coincident(g12,g27)
    c: Coincident(g10,g26)
    c: Coincident(g11,g26)
    c: Tangent(g9,g30) = -1.5708
    c: Tangent(g10,g30) = -1.5708
    c: Tangent(g0,g31) = 1.5708
    c: Tangent(g17,g31) = 1.5708
    c: Tangent(g16,g32) = -1.5708
    c: Tangent(g15,g32) = -1.5708
    c: Tangent(g15,g33) = 1.5708
    c: Tangent(g14,g33) = 1.5708
    c: Tangent(g14,g34) = -1.5708
    c: Tangent(g13,g34) = -1.5708
    c: Tangent(g11,g35) = 1.5708
    c: Tangent(g12,g35) = 1.5708
FEATURE [PartDesign::Pocket] Pocket
  BaseFeature = -> Pad
  Direction = (0,0,-1)
  Length = 2
  Length2 = 5
  Placement = pos=(0,0,8) rot=(0,0,1;0rad)
  Profile = -> Sketch058
  ReferenceAxis = -> Sketch058 [N_Axis]
  Suppressed = false
  Type = 0
FEATURE [PartDesign::Fillet] Fillet006  label="On Off Border Radius"
  Base = -> Fillet [Edge583]
  BaseFeature = -> Fillet
  Placement = pos=(0,0,8) rot=(0,0,1;0rad)
  Radius = 1
  SupportTransform = false
  Suppressed = false
  UseAllEdges = false
FEATURE [Sketcher::SketchObject] Sketch079
  ArcFitTolerance = 0
  FullyConstrained = false
  MakeInternals = false
  MapMode = 5
  Placement = pos=(0,0,18) rot=(1,0,0;3.14159rad)
  sketch-geometry (15):
    g0: Circle CenterX=18.6 CenterY=-18.76 CenterZ=0 NormalX=0 NormalY=0 NormalZ=1 AngleXU=0 Radius=1.7
    g1: Circle CenterX=18.61 CenterY=-37.51 CenterZ=0 NormalX=0 NormalY=0 NormalZ=1 AngleXU=0 Radius=1.7
    g2: Circle CenterX=94.55 CenterY=-41.5 CenterZ=0 NormalX=0 NormalY=0 NormalZ=1 AngleXU=0 Radius=1.7
    g3: Circle CenterX=108.3 CenterY=6.24 CenterZ=0 NormalX=0 NormalY=0 NormalZ=1 AngleXU=0 Radius=1.7
    g4: Circle CenterX=61.84 CenterY=-1.51 CenterZ=0 NormalX=0 NormalY=0 NormalZ=1 AngleXU=0 Radius=1.7
    g5: Circle CenterX=18.6 CenterY=-18.76 CenterZ=0 NormalX=0 NormalY=0 NormalZ=1 AngleXU=0 Radius=3.33137
    g6: Circle CenterX=18.61 CenterY=-37.51 CenterZ=0 NormalX=0 NormalY=0 NormalZ=1 AngleXU=0 Radius=3.30009
    g7: Circle CenterX=61.84 CenterY=-1.51 CenterZ=0 NormalX=0 NormalY=0 NormalZ=1 AngleXU=0 Radius=3.39571
    g8: Circle CenterX=108.3 CenterY=6.24 CenterZ=0 NormalX=0 NormalY=0 NormalZ=1 AngleXU=0 Radius=3.4573
    g9: ArcOfCircle CenterX=94.55 CenterY=-41.5 CenterZ=0 NormalX=0 NormalY=0 NormalZ=1 AngleXU=0 Radius=3.38574 StartAngle=5.97097 EndAngle=8.61296
    g10: LineSegment StartX=97.27 StartY=-42.54 StartZ=0 EndX=97.27 EndY=-43.5161 EndZ=0
    g11: ArcOfCircle CenterX=94.5506 CenterY=-41.4991 CenterZ=0 NormalX=0 NormalY=0 NormalZ=1 AngleXU=0 Radius=3.38581 StartAngle=2.62271 EndAngle=5.64499
    g12: LineSegment StartX=97.7721 StartY=-42.54 StartZ=0 EndX=97.27 EndY=-42.54 EndZ=0
    g13: LineSegment StartX=92.22 StartY=-39.0435 StartZ=0 EndX=92.22 EndY=-39.82 EndZ=0
    g14: LineSegment StartX=91.6105 StartY=-39.82 StartZ=0 EndX=92.22 EndY=-39.82 EndZ=0
  constraints (19):
    c: Coincident(g5,g0)
    c: Coincident(g6,g1)
    c: Coincident(g7,g4)
    c: Coincident(g8,g3)
    c: Vertical(g10)
    c: Coincident(g11,g10)
    c: Coincident(g12,g9)
    c: Coincident(g12,g10)
    c: Horizontal(g12)
    c: Diameter(g1) = 3.4
    c: Diameter(g0) = 3.4
    c: Diameter(g4) = 3.4
    c: Diameter(g2) = 3.4
    c: Diameter(g3) = 3.4
    c: Coincident(g13,g9)
    c: Vertical(g13)
    c: Coincident(g14,g11)
    c: Horizontal(g14)
    c: Coincident(g14,g13)
FEATURE [Sketcher::SketchObject] Sketch119
  ArcFitTolerance = 0
  AttachmentSupport = -> [Pocket]
  FullyConstrained = false
  MakeInternals = false
  MapMode = 5
  Placement = pos=(0,0,10) rot=(0,0,1;0rad)
  sketch-geometry (5):
    g0: Circle CenterX=18.6105 CenterY=37.4905 CenterZ=0 NormalX=0 NormalY=0 NormalZ=1 AngleXU=0 Radius=4
    g1: Circle CenterX=18.5894 CenterY=18.7479 CenterZ=0 NormalX=0 NormalY=0 NormalZ=1 AngleXU=0 Radius=4
    g2: Circle CenterX=61.8331 CenterY=1.49994 CenterZ=0 NormalX=0 NormalY=0 NormalZ=1 AngleXU=0 Radius=4
    g3: Circle CenterX=108.311 CenterY=-6.25509 CenterZ=0 NormalX=0 NormalY=0 NormalZ=1 AngleXU=0 Radius=4
    g4: Circle CenterX=94.5439 CenterY=41.487 CenterZ=0 NormalX=0 NormalY=0 NormalZ=1 AngleXU=0 Radius=4
  constraints (5):
    c: Radius(g0) = 4
    c: Radius(g1) = 4
    c: Radius(g2) = 4
    c: Radius(g3) = 4
    c: Radius(g4) = 4
FEATURE [PartDesign::Pad] Pad030
  BaseFeature = -> Pocket
  Direction = (0,0,1)
  Length = 9
  Length2 = 10
  Placement = pos=(0,0,8) rot=(0,0,1;0rad)
  Profile = -> Sketch119
  ReferenceAxis = -> Sketch119 [N_Axis]
  Suppressed = false
  Type = 0
FEATURE [Sketcher::SketchObject] Sketch118
  ArcFitTolerance = 0
  AttachmentOffset = pos=(0,0,0) rot=(1,0,0;3.14159rad)
  AttachmentSupport = -> [Pad030]
  FullyConstrained = false
  MakeInternals = false
  MapMode = 5
  Placement = pos=(0,0,8) rot=(0,0,1;0rad)
  sketch-geometry (13):
    g0: Circle [constr] CenterX=61.8331 CenterY=1.49994 CenterZ=0 NormalX=0 NormalY=0 NormalZ=1 AngleXU=0 Radius=1.69083
    g1: Circle [constr] CenterX=108.311 CenterY=-6.25509 CenterZ=0 NormalX=0 NormalY=0 NormalZ=1 AngleXU=0 Radius=1.7012
    g2: Circle [constr] CenterX=18.5894 CenterY=18.7479 CenterZ=0 NormalX=0 NormalY=0 NormalZ=1 AngleXU=0 Radius=2.25
    g3: Circle [constr] CenterX=18.6105 CenterY=37.4905 CenterZ=0 NormalX=0 NormalY=0 NormalZ=1 AngleXU=0 Radius=2.25
    g4: Circle [constr] CenterX=61.8331 CenterY=1.49994 CenterZ=0 NormalX=0 NormalY=0 NormalZ=1 AngleXU=0 Radius=2.25
    g5: Circle [constr] CenterX=108.311 CenterY=-6.25509 CenterZ=0 NormalX=0 NormalY=0 NormalZ=1 AngleXU=0 Radius=2.25
    g6: Circle [constr] CenterX=94.5439 CenterY=41.487 CenterZ=0 NormalX=0 NormalY=0 NormalZ=1 AngleXU=0 Radius=2.25
    g7: Circle [constr] CenterX=94.5439 CenterY=41.487 CenterZ=0 NormalX=0 NormalY=0 NormalZ=1 AngleXU=0 Radius=3
    g8: Circle CenterX=18.6105 CenterY=37.4905 CenterZ=0 NormalX=0 NormalY=0 NormalZ=1 AngleXU=0 Radius=3
    g9: Circle CenterX=18.5894 CenterY=18.7479 CenterZ=0 NormalX=0 NormalY=0 NormalZ=1 AngleXU=0 Radius=3
    g10: Circle CenterX=61.8331 CenterY=1.49994 CenterZ=0 NormalX=0 NormalY=0 NormalZ=1 AngleXU=0 Radius=3
    g11: Circle CenterX=108.311 CenterY=-6.25509 CenterZ=0 NormalX=0 NormalY=0 NormalZ=1 AngleXU=0 Radius=3
    g12: Circle CenterX=94.5439 CenterY=41.487 CenterZ=0 NormalX=0 NormalY=0 NormalZ=1 AngleXU=0 Radius=3
  constraints (19):
    c: Radius(g2) = 2.25
    c: Radius(g3) = 2.25
    c: Coincident(g4,g0)
    c: Coincident(g5,g1)
    c: Radius(g6) = 2.25
    c: Radius(g4) = 2.25
    c: Radius(g5) = 2.25
    c: Coincident(g7,g6)
    c: Radius(g7) = 3
    c: Coincident(g8,g3)
    c: Radius(g8) = 3
    c: Coincident(g9,g2)
    c: Radius(g9) = 3
    c: Coincident(g10,g0)
    c: Radius(g10) = 3
    c: Coincident(g11,g1)
    c: Radius(g11) = 3
    c: Coincident(g12,g6)
    c: Radius(g12) = 3
FEATURE [PartDesign::Pad] Pad032  label="PCB Support"
  BaseFeature = -> Fillet006
  Direction = (0,0,-1)
  Length = 1.5
  Length2 = 10
  Placement = pos=(0,0,8) rot=(0,0,1;0rad)
  Profile = -> Sketch079
  ReferenceAxis = -> Sketch079 [N_Axis]
  Suppressed = false
  Type = 0
FEATURE [Sketcher::SketchObject] Sketch126
  ArcFitTolerance = 0
  AttachmentSupport = -> [Pad032]
  ExternalGeometry = -> [Pad032]
  FullyConstrained = true
  MakeInternals = false
  MapMode = 5
  Placement = pos=(0,0,16.5) rot=(1,0,0;3.14159rad)
  sketch-geometry (5):
    g0: Circle CenterX=94.55 CenterY=-41.5 CenterZ=0 NormalX=0 NormalY=0 NormalZ=1 AngleXU=0 Radius=1.7
    g1: Circle CenterX=18.61 CenterY=-37.51 CenterZ=0 NormalX=0 NormalY=0 NormalZ=1 AngleXU=0 Radius=1.7
    g2: Circle CenterX=18.6 CenterY=-18.76 CenterZ=0 NormalX=0 NormalY=0 NormalZ=1 AngleXU=0 Radius=1.7
    g3: Circle CenterX=61.84 CenterY=-1.51 CenterZ=0 NormalX=0 NormalY=0 NormalZ=1 AngleXU=0 Radius=1.7
    g4: Circle CenterX=108.3 CenterY=6.24 CenterZ=0 NormalX=0 NormalY=0 NormalZ=1 AngleXU=0 Radius=1.7
  constraints (10):
    c: Coincident(g0,g-7)
    c: Equal(g0,g-7)
    c: Coincident(g1,g-6)
    c: Equal(g1,g-6)
    c: Coincident(g2,g-5)
    c: Equal(g2,g-5)
    c: Coincident(g3,g-3)
    c: Equal(g3,g-3)
    c: Coincident(g4,g-4)
    c: Equal(g4,g-4)
FEATURE [PartDesign::Pocket] Pocket031  label="Columns Hole"
  BaseFeature = -> Pad032
  Direction = (0,0,1)
  Length = 3
  Length2 = 5
  Placement = pos=(0,0,8) rot=(0,0,1;0rad)
  Profile = -> Sketch126
  ReferenceAxis = -> Sketch126 [N_Axis]
  Suppressed = false
  Type = 0
FEATURE [Sketcher::SketchObject] Sketch128
  ArcFitTolerance = 0
  AttachmentSupport = -> [XY_Plane]
  FullyConstrained = false
  MakeInternals = false
  MapMode = 5
  sketch-geometry (10):
    g0: LineSegment StartX=20.7746 StartY=-17.9889 StartZ=0 EndX=36.9746 EndY=-17.9889 EndZ=0
    g1: LineSegment StartX=37.9746 StartY=-18.9889 StartZ=0 EndX=37.9746 EndY=-50.3889 EndZ=0
    g2: LineSegment StartX=36.9746 StartY=-51.3889 StartZ=0 EndX=20.7746 EndY=-51.3889 EndZ=0
    g3: LineSegment StartX=19.7746 StartY=-50.3889 StartZ=0 EndX=19.7746 EndY=-18.9889 EndZ=0
    g4: ArcOfCircle CenterX=36.9746 CenterY=-50.3889 CenterZ=0 NormalX=0 NormalY=0 NormalZ=1 AngleXU=0 Radius=1 StartAngle=4.71239 EndAngle=6.28319
    g5: ArcOfCircle CenterX=20.7746 CenterY=-50.3889 CenterZ=0 NormalX=0 NormalY=0 NormalZ=1 AngleXU=0 Radius=1 StartAngle=3.14159 EndAngle=4.71239
    g6: ArcOfCircle CenterX=20.7746 CenterY=-18.9889 CenterZ=0 NormalX=0 NormalY=0 NormalZ=1 AngleXU=0 Radius=1 StartAngle=1.5708 EndAngle=3.14159
    g7: ArcOfCircle CenterX=36.9746 CenterY=-18.9889 CenterZ=0 NormalX=0 NormalY=0 NormalZ=1 AngleXU=0 Radius=1 StartAngle=0 EndAngle=1.5708
    g8: LineSegment [constr] StartX=28.6455 StartY=-51.3889 StartZ=0 EndX=28.6455 EndY=-17.9889 EndZ=0
    g9: LineSegment [constr] StartX=19.7746 StartY=-47.1868 StartZ=0 EndX=37.9746 EndY=-47.1868 EndZ=0
  constraints (24):
    c: Horizontal(g0)
    c: Horizontal(g2)
    c: Vertical(g1)
    c: Vertical(g3)
    c: Tangent(g1,g4) = 1.5708
    c: Tangent(g2,g4) = 1.5708
    c: Tangent(g3,g5) = 1.5708
    c: Tangent(g2,g5) = 1.5708
    c: Tangent(g0,g6) = 1.5708
    c: Tangent(g3,g6) = 1.5708
    c: Tangent(g0,g7) = 1.5708
    c: Tangent(g1,g7) = 1.5708
    c: Radius(g7) = 1
    c: Radius(g6) = 1
    c: Radius(g5) = 1
    c: Radius(g4) = 1
    c: PointOnObject(g8,g2)
    c: PointOnObject(g8,g0)
    c: Vertical(g8)
    c: PointOnObject(g9,g3)
    c: PointOnObject(g9,g1)
    c: Horizontal(g9)
    c: Distance(g8) = 33.4
    c: Distance(g9) = 18.2
FEATURE [PartDesign::Pad] Pad034
  Direction = (0,0,1)
  Length = 1.6
  Length2 = 10
  Profile = -> Sketch128
  ReferenceAxis = -> Sketch128 [N_Axis]
  Suppressed = false
  Type = 0
FEATURE [Sketcher::SketchObject] Sketch130
  ArcFitTolerance = 0
  AttachmentSupport = -> [Pad034]
  ExternalGeometry = -> [Pad034]
  FullyConstrained = true
  MakeInternals = false
  MapMode = 5
  Placement = pos=(0,0,0) rot=(1,0,0;3.14159rad)
  sketch-geometry (6):
    g0: LineSegment StartX=33.3746 StartY=24.0889 StartZ=0 EndX=24.3746 EndY=24.0889 EndZ=0
    g1: LineSegment [constr] StartX=24.3746 StartY=24.0889 StartZ=0 EndX=19.7746 EndY=24.0889 EndZ=0
    g2: LineSegment StartX=24.3746 StartY=24.0889 StartZ=0 EndX=24.3746 EndY=17.9889 EndZ=0
    g3: LineSegment StartX=33.3746 StartY=24.0889 StartZ=0 EndX=33.3746 EndY=17.9889 EndZ=0
    g4: LineSegment StartX=24.3746 StartY=17.9889 StartZ=0 EndX=33.3746 EndY=17.9889 EndZ=0
    g5: LineSegment [constr] StartX=33.3746 StartY=24.0889 StartZ=0 EndX=37.9746 EndY=24.0889 EndZ=0
  constraints (18):
    c: Horizontal(g0)
    c: Coincident(g1,g0)
    c: PointOnObject(g1,g-5)
    c: Horizontal(g1)
    c: Distance(g0) = 9
    c: Coincident(g2,g0)
    c: PointOnObject(g2,g-6)
    c: Vertical(g2)
    c: Coincident(g3,g0)
    c: PointOnObject(g3,g-6)
    c: Vertical(g3)
    c: Distance(g3) = 6.1
    c: Coincident(g4,g2)
    c: Coincident(g4,g3)
    c: Coincident(g5,g0)
    c: PointOnObject(g5,g-4)
    c: Horizontal(g5)
    c: Equal(g5,g1)
FEATURE [PartDesign::Pocket] Pocket032
  BaseFeature = -> Pad034
  Direction = (0,0,1)
  Length = 5
  Length2 = 5
  Profile = -> Sketch130
  ReferenceAxis = -> Sketch130 [N_Axis]
  Suppressed = false
  Type = 1
FEATURE [Sketcher::SketchObject] Sketch131
  ArcFitTolerance = 0
  AttachmentSupport = -> [Pocket032]
  ExternalGeometry = -> [Pocket032]
  FullyConstrained = false
  MakeInternals = false
  MapMode = 5
  Placement = pos=(0,-24.0889,0) rot=(0,0.707107,0.707107;3.14159rad)
  sketch-geometry (11):
    g0: ArcOfCircle CenterX=-32.8504 CenterY=0.524237 CenterZ=0 NormalX=0 NormalY=0 NormalZ=1 AngleXU=0 Radius=0.524237 StartAngle=3.14159 EndAngle=4.71239
    g1: LineSegment StartX=-33.3746 StartY=0.524237 StartZ=0 EndX=-33.3746 EndY=2.77576 EndZ=0
    g2: ArcOfCircle CenterX=-32.8504 CenterY=2.77576 CenterZ=0 NormalX=0 NormalY=0 NormalZ=1 AngleXU=0 Radius=0.524237 StartAngle=1.5708 EndAngle=3.14159
    g3: LineSegment StartX=-32.8504 StartY=3.3 StartZ=0 EndX=-24.8989 EndY=3.3 EndZ=0
    g4: ArcOfCircle CenterX=-24.8989 CenterY=2.77576 CenterZ=0 NormalX=0 NormalY=0 NormalZ=1 AngleXU=0 Radius=0.524237 StartAngle=0 EndAngle=1.5708
    g5: LineSegment StartX=-24.3746 StartY=2.77576 StartZ=0 EndX=-24.3746 EndY=0.524237 EndZ=0
    g6: ArcOfCircle CenterX=-24.8989 CenterY=0.524237 CenterZ=0 NormalX=0 NormalY=0 NormalZ=1 AngleXU=0 Radius=0.524237 StartAngle=4.71239 EndAngle=6.28319
    g7: LineSegment StartX=-24.8989 StartY=0 StartZ=0 EndX=-32.8504 EndY=0 EndZ=0
    g8: GeomPoint [constr] X=-33.3746 Y=0 Z=0
    g9: GeomPoint [constr] X=-24.3746 Y=3.3 Z=0
    g10: LineSegment [constr] StartX=-28.8746 StartY=0 StartZ=0 EndX=-28.8746 EndY=3.3 EndZ=0
  constraints (24):
    c: Tangent(g0,g1) = 1.5708
    c: Tangent(g1,g2) = 1.5708
    c: Tangent(g2,g3) = 1.5708
    c: Tangent(g3,g4) = 1.5708
    c: Tangent(g4,g5) = 1.5708
    c: Tangent(g5,g6) = 1.5708
    c: Tangent(g6,g7) = 1.5708
    c: Tangent(g7,g0) = 1.5708
    c: Horizontal(g3)
    c: Horizontal(g7)
    c: Vertical(g1)
    c: Vertical(g5)
    c: Equal(g0,g2)
    c: Equal(g2,g4)
    c: Equal(g4,g6)
    c: PointOnObject(g8,g1)
    c: PointOnObject(g8,g7)
    c: PointOnObject(g9,g3)
    c: PointOnObject(g9,g5)
    c: Coincident(g8,g-3)
    c: PointOnObject(g10,g7)
    c: PointOnObject(g10,g3)
    c: Vertical(g10)
    c: Distance(g10) = 3.3
FEATURE [PartDesign::Pad] Pad035
  BaseFeature = -> Pocket032
  Direction = (0,1,-2e-16)
  Length = 6.6
  Length2 = 10
  Profile = -> Sketch131
  ReferenceAxis = -> Sketch131 [N_Axis]
  Suppressed = false
  Type = 0
FEATURE [Sketcher::SketchObject] Sketch132
  ArcFitTolerance = 0
  AttachmentSupport = -> [Pad035]
  ExternalGeometry = -> [Pad035]
  FullyConstrained = false
  MakeInternals = false
  MapMode = 5
  Placement = pos=(0,0,1.6) rot=(0,0,1;0rad)
  sketch-geometry (7):
    g0: LineSegment [constr] StartX=28.8746 StartY=-51.3889 StartZ=0 EndX=28.8746 EndY=-42.1889 EndZ=0
    g1: LineSegment StartX=25.4746 StartY=-42.1889 StartZ=0 EndX=32.2746 EndY=-42.1889 EndZ=0
    g2: LineSegment StartX=32.2746 StartY=-42.1889 StartZ=0 EndX=32.2746 EndY=-35.3889 EndZ=0
    g3: LineSegment StartX=32.2746 StartY=-35.3889 StartZ=0 EndX=25.4746 EndY=-35.3889 EndZ=0
    g4: LineSegment StartX=25.4746 StartY=-35.3889 StartZ=0 EndX=25.4746 EndY=-42.1889 EndZ=0
    g5: LineSegment [constr] StartX=25.4746 StartY=-42.1889 StartZ=0 EndX=19.7746 EndY=-42.1889 EndZ=0
    g6: LineSegment [constr] StartX=32.2746 StartY=-42.1889 StartZ=0 EndX=37.9746 EndY=-42.1889 EndZ=0
  constraints (21):
    c: PointOnObject(g0,g-3)
    c: Vertical(g0)
    c: Coincident(g1,g2)
    c: Coincident(g2,g3)
    c: Coincident(g3,g4)
    c: Coincident(g4,g1)
    c: Horizontal(g1)
    c: Horizontal(g3)
    c: Vertical(g2)
    c: Vertical(g4)
    c: Distance(g4) = 6.8
    c: Distance(g1) = 6.8
    c: PointOnObject(g0,g1)
    c: Coincident(g5,g1)
    c: PointOnObject(g5,g-4)
    c: Horizontal(g5)
    c: Coincident(g6,g1)
    c: PointOnObject(g6,g-5)
    c: Horizontal(g6)
    c: Equal(g5,g6)
    c: Distance(g0) = 9.2
FEATURE [PartDesign::Pad] Pad036
  BaseFeature = -> Pad035
  Direction = (0,0,1)
  Length = 1.1
  Length2 = 10
  Profile = -> Sketch132
  ReferenceAxis = -> Sketch132 [N_Axis]
  Suppressed = false
  Type = 0
FEATURE [Sketcher::SketchObject] Sketch133
  ArcFitTolerance = 0
  AttachmentSupport = -> [Pad036]
  FullyConstrained = false
  MakeInternals = false
  MapMode = 5
  Placement = pos=(0,7e-16,3.3) rot=(0,0,1;0rad)
  sketch-geometry (16):
    g0: LineSegment StartX=21.2562 StartY=-49.8327 StartZ=0 EndX=21.2562 EndY=-36.9147 EndZ=0
    g1: ArcOfCircle CenterX=24.66 CenterY=-47.5055 CenterZ=0 NormalX=0 NormalY=0 NormalZ=1 AngleXU=0 Radius=1.12391 StartAngle=3.14159 EndAngle=4.71239
    g2: ArcOfCircle CenterX=33.4356 CenterY=-47.703 CenterZ=0 NormalX=0 NormalY=0 NormalZ=1 AngleXU=0 Radius=0.92638 StartAngle=4.71239 EndAngle=6.28319
    g3: ArcOfCircle CenterX=22.4318 CenterY=-49.8327 CenterZ=0 NormalX=0 NormalY=0 NormalZ=1 AngleXU=0 Radius=1.17565 StartAngle=3.14159 EndAngle=4.71239
    g4: ArcOfCircle CenterX=35.3926 CenterY=-49.8189 CenterZ=0 NormalX=0 NormalY=0 NormalZ=1 AngleXU=0 Radius=1.18945 StartAngle=4.71239 EndAngle=6.28319
    g5: LineSegment StartX=36.582 StartY=-36.7335 StartZ=0 EndX=36.582 EndY=-49.8189 EndZ=0
    g6: ArcOfCircle CenterX=22.0316 CenterY=-36.9147 CenterZ=0 NormalX=0 NormalY=0 NormalZ=1 AngleXU=0 Radius=0.775438 StartAngle=1.5708 EndAngle=3.14159
    g7: ArcOfCircle CenterX=22.8657 CenterY=-36.8097 CenterZ=0 NormalX=0 NormalY=0 NormalZ=1 AngleXU=0 Radius=0.670451 StartAngle=0 EndAngle=1.5708
    g8: ArcOfCircle CenterX=34.9928 CenterY=-36.7701 CenterZ=0 NormalX=0 NormalY=0 NormalZ=1 AngleXU=0 Radius=0.630815 StartAngle=1.5708 EndAngle=3.14159
    g9: ArcOfCircle CenterX=35.9878 CenterY=-36.7335 CenterZ=0 NormalX=0 NormalY=0 NormalZ=1 AngleXU=0 Radius=0.594269 StartAngle=0 EndAngle=1.5708
    g10: LineSegment StartX=22.4318 StartY=-51.0083 StartZ=0 EndX=35.3926 EndY=-51.0083 EndZ=0
    g11: LineSegment StartX=24.66 StartY=-48.6294 StartZ=0 EndX=33.4356 EndY=-48.6294 EndZ=0
    g12: LineSegment StartX=22.0316 StartY=-36.1393 StartZ=0 EndX=22.8657 EndY=-36.1393 EndZ=0
    g13: LineSegment StartX=34.9928 StartY=-36.1393 StartZ=0 EndX=35.9878 EndY=-36.1393 EndZ=0
    g14: LineSegment StartX=34.362 StartY=-36.7701 StartZ=0 EndX=34.362 EndY=-47.703 EndZ=0
    g15: LineSegment StartX=23.5361 StartY=-47.5055 StartZ=0 EndX=23.5361 EndY=-36.8097 EndZ=0
  constraints (24):
    c: Vertical(g0)
    c: Tangent(g0,g3) = 1.5708
    c: Coincident(g5,g4)
    c: Vertical(g5)
    c: Tangent(g0,g6) = 1.5708
    c: Tangent(g5,g9) = 1.5708
    c: Coincident(g10,g3)
    c: Coincident(g10,g4)
    c: Horizontal(g10)
    c: Coincident(g11,g1)
    c: Coincident(g11,g2)
    c: Horizontal(g11)
    c: Coincident(g12,g6)
    c: Coincident(g12,g7)
    c: Horizontal(g12)
    c: Coincident(g13,g8)
    c: Coincident(g13,g9)
    c: Horizontal(g13)
    c: Coincident(g14,g8)
    c: Coincident(g14,g2)
    c: Vertical(g14)
    c: Coincident(g15,g1)
    c: Coincident(g15,g7)
    c: Vertical(g15)
FEATURE [PartDesign::Pad] Pad037
  BaseFeature = -> Pad036
  Direction = (0,0,1)
  Length = 3
  Length2 = 10
  Profile = -> Sketch133
  ReferenceAxis = -> Sketch133 [N_Axis]
  Reversed = true
  Suppressed = false
  Type = 0
FEATURE [PartDesign::Body] Body  label="NiceNano"
  AllowCompound = false
  Group = -> [Sketch128,Pad034,Sketch130,Pocket032,Sketch131,Pad035,Sketch132,Pad036,Sketch133,Pad037]
  Origin = -> Origin
  Tip = -> Pad037
FEATURE [PartDesign::Pocket] Pocket028
  BaseFeature = -> Pad030
  Direction = (0,-1e-16,-1)
  Length = 10
  Length2 = 5
  Placement = pos=(0,0,8) rot=(0,0,1;0rad)
  Profile = -> Sketch118
  ReferenceAxis = -> Sketch118 [N_Axis]
  Reversed = true
  Suppressed = false
  Type = 0
FEATURE [Sketcher::SketchObject] Sketch120
  ArcFitTolerance = 0
  AttachmentSupport = -> [Pocket028]
  ExternalGeometry = -> [Pocket028]
  FullyConstrained = true
  MakeInternals = false
  MapMode = 5
  Placement = pos=(0,0,19) rot=(0,0,1;0rad)
  sketch-geometry (5):
    g0: Circle CenterX=18.5894 CenterY=18.7479 CenterZ=0 NormalX=0 NormalY=0 NormalZ=1 AngleXU=0 Radius=1.9
    g1: Circle CenterX=18.6105 CenterY=37.4905 CenterZ=0 NormalX=0 NormalY=0 NormalZ=1 AngleXU=0 Radius=1.9
    g2: Circle CenterX=94.5439 CenterY=41.487 CenterZ=0 NormalX=0 NormalY=0 NormalZ=1 AngleXU=0 Radius=1.9
    g3: Circle CenterX=108.311 CenterY=-6.25509 CenterZ=0 NormalX=0 NormalY=0 NormalZ=1 AngleXU=0 Radius=1.9
    g4: Circle CenterX=61.8331 CenterY=1.49994 CenterZ=0 NormalX=0 NormalY=0 NormalZ=1 AngleXU=0 Radius=1.9
  constraints (10):
    c: Coincident(g0,g-3)
    c: Radius(g0) = 1.9
    c: Coincident(g1,g-4)
    c: Coincident(g2,g-5)
    c: Coincident(g3,g-6)
    c: Coincident(g4,g-7)
    c: Radius(g1) = 1.9
    c: Radius(g2) = 1.9
    c: Radius(g3) = 1.9
    c: Radius(g4) = 1.9
FEATURE [PartDesign::Pad] Pad031
  BaseFeature = -> Pocket028
  Direction = (0,0,1)
  Length = 1.5
  Length2 = 10
  Placement = pos=(0,0,8) rot=(0,0,1;0rad)
  Profile = -> Sketch120
  ReferenceAxis = -> Sketch120 [N_Axis]
  Suppressed = false
  Type = 0
FEATURE [Sketcher::SketchObject] Sketch121
  ArcFitTolerance = 0
  AttachmentSupport = -> [Pad031]
  ExternalGeometry = -> [Pad031]
  FullyConstrained = true
  MakeInternals = false
  MapMode = 5
  Placement = pos=(0,0,20.5) rot=(0,0,1;0rad)
  sketch-geometry (5):
    g0: Circle CenterX=18.6105 CenterY=37.4905 CenterZ=0 NormalX=0 NormalY=0 NormalZ=1 AngleXU=0 Radius=1.39
    g1: Circle CenterX=18.5894 CenterY=18.7479 CenterZ=0 NormalX=0 NormalY=0 NormalZ=1 AngleXU=0 Radius=1.39
    g2: Circle CenterX=94.5439 CenterY=41.487 CenterZ=0 NormalX=0 NormalY=0 NormalZ=1 AngleXU=0 Radius=1.39
    g3: Circle CenterX=61.8331 CenterY=1.49994 CenterZ=0 NormalX=0 NormalY=0 NormalZ=1 AngleXU=0 Radius=1.39
    g4: Circle CenterX=108.311 CenterY=-6.25509 CenterZ=0 NormalX=0 NormalY=0 NormalZ=1 AngleXU=0 Radius=1.39
  constraints (10):
    c: Coincident(g0,g-3)
    c: Coincident(g1,g-5)
    c: Coincident(g2,g-4)
    c: Coincident(g3,g-6)
    c: Coincident(g4,g-7)
    c: Radius(g0) = 1.39
    c: Radius(g1) = 1.39
    c: Radius(g3) = 1.39
    c: Radius(g4) = 1.39
    c: Radius(g2) = 1.39
FEATURE [PartDesign::Pocket] Pocket029
  BaseFeature = -> Pad031
  Direction = (0,0,-1)
  Length = 5
  Length2 = 5
  Placement = pos=(0,0,8) rot=(0,0,1;0rad)
  Profile = -> Sketch121
  ReferenceAxis = -> Sketch121 [N_Axis]
  Suppressed = false
  Type = 1
FEATURE [Sketcher::SketchObject] Sketch125
  ArcFitTolerance = 0
  AttachmentSupport = -> [Pocket029]
  FullyConstrained = false
  MakeInternals = false
  MapMode = 5
  Placement = pos=(0,0,8) rot=(1,0,0;3.14159rad)
  sketch-geometry (5):
    g0: Circle CenterX=5.4195 CenterY=-5.47064 CenterZ=0 NormalX=0 NormalY=0 NormalZ=1 AngleXU=0 Radius=5
    g1: Circle CenterX=5.4195 CenterY=-50.997 CenterZ=0 NormalX=0 NormalY=0 NormalZ=1 AngleXU=0 Radius=5
    g2: Circle CenterX=69.7206 CenterY=-25.9633 CenterZ=0 NormalX=0 NormalY=0 NormalZ=1 AngleXU=0 Radius=5
    g3: Circle CenterX=115.074 CenterY=17.0478 CenterZ=0 NormalX=0 NormalY=0 NormalZ=1 AngleXU=0 Radius=5
    g4: Circle CenterX=123.886 CenterY=-50.0179 CenterZ=0 NormalX=0 NormalY=0 NormalZ=1 AngleXU=0 Radius=5
  constraints (6):
    c: Radius(g0) = 5
    c: Vertical(g0,g1)
    c: Radius(g1) = 5
    c: Radius(g2) = 5
    c: Radius(g3) = 5
    c: Radius(g4) = 5
FEATURE [Sketcher::SketchObject] Sketch135
  ArcFitTolerance = 0
  AttachmentSupport = -> [XY_Plane010]
  FullyConstrained = false
  MakeInternals = false
  MapMode = 5
  sketch-geometry (1):
    g0: Circle CenterX=-60.9814 CenterY=52.6072 CenterZ=0 NormalX=0 NormalY=0 NormalZ=1 AngleXU=0 Radius=1.9
  constraints (1):
    c: Radius(g0) = 1.9
FEATURE [PartDesign::Pad] Pad038
  Direction = (0,0,1)
  Length = 0.9
  Length2 = 10
  Profile = -> Sketch135
  ReferenceAxis = -> Sketch135 [N_Axis]
  Suppressed = false
  Type = 0
FEATURE [Sketcher::SketchObject] Sketch136
  ArcFitTolerance = 0
  AttachmentSupport = -> [Pad038]
  ExternalGeometry = -> [Pad038]
  FullyConstrained = true
  MakeInternals = false
  MapMode = 5
  Placement = pos=(0,0,0.9) rot=(0,0,1;0rad)
  sketch-geometry (1):
    g0: Circle CenterX=-60.9814 CenterY=52.6072 CenterZ=0 NormalX=0 NormalY=0 NormalZ=1 AngleXU=0 Radius=0.9
  constraints (2):
    c: Coincident(g0,g-3)
    c: Radius(g0) = 0.9
FEATURE [PartDesign::Pad] Pad039
  BaseFeature = -> Pad038
  Direction = (0,0,1)
  Length = 4.9
  Length2 = 10
  Profile = -> Sketch136
  ReferenceAxis = -> Sketch136 [N_Axis]
  Suppressed = false
  Type = 0
FEATURE [PartDesign::Fillet] Fillet011
  Base = -> Pad039 [Edge3,Edge2]
  BaseFeature = -> Pad039
  Radius = 0.2
  SupportTransform = false
  Suppressed = false
  UseAllEdges = false
FEATURE [Sketcher::SketchObject] Sketch137
  ArcFitTolerance = 0
  AttachmentSupport = -> [Fillet011]
  ExternalGeometry = -> [Fillet011]
  FullyConstrained = false
  MakeInternals = false
  MapMode = 5
  Placement = pos=(0,0,0) rot=(1,0,0;3.14159rad)
  sketch-geometry (7):
    g0: LineSegment StartX=-60.2558 StartY=-53.1161 StartZ=0 EndX=-60.1779 EndY=-52.2332 EndZ=0
    g1: LineSegment StartX=-60.1779 StartY=-52.2332 StartZ=0 EndX=-60.9035 EndY=-51.7243 EndZ=0
    g2: LineSegment StartX=-60.9035 StartY=-51.7243 StartZ=0 EndX=-61.7071 EndY=-52.0982 EndZ=0
    g3: LineSegment StartX=-61.7071 StartY=-52.0982 StartZ=0 EndX=-61.785 EndY=-52.9811 EndZ=0
    g4: LineSegment StartX=-61.785 StartY=-52.9811 StartZ=0 EndX=-61.0594 EndY=-53.49 EndZ=0
    g5: LineSegment StartX=-61.0594 StartY=-53.49 StartZ=0 EndX=-60.2558 EndY=-53.1161 EndZ=0
    g6: Circle [constr] CenterX=-60.9814 CenterY=-52.6072 CenterZ=0 NormalX=0 NormalY=0 NormalZ=1 AngleXU=0 Radius=0.886307
  constraints (14):
    c: Coincident(g0,g1)
    c: Coincident(g1,g2)
    c: Coincident(g2,g3)
    c: Coincident(g3,g4)
    c: Coincident(g4,g5)
    c: Coincident(g5,g0)
    c: Equal(g0, g1-g5) x5
    c: PointOnObject(g0,g6)
    c: PointOnObject(g1,g6)
    c: PointOnObject(g2,g6)
    c: PointOnObject(g3,g6)
    c: PointOnObject(g4,g6)
    c: PointOnObject(g5,g6)
    c: Coincident(g6,g-3)
FEATURE [PartDesign::Pocket] Pocket034
  BaseFeature = -> Fillet011
  Direction = (0,0,1)
  Length = 0.6
  Length2 = 5
  Profile = -> Sketch137
  ReferenceAxis = -> Sketch137 [N_Axis]
  Suppressed = false
  Type = 0
FEATURE [PartDesign::Fillet] Fillet012
  Base = -> Pocket034 [Edge28]
  BaseFeature = -> Pocket034
  Radius = 0.2
  SupportTransform = false
  Suppressed = false
  UseAllEdges = false
FEATURE [PartDesign::Body] Body010  label="Tornillo"
  AllowCompound = false
  Group = -> [Sketch135,Pad038,Sketch136,Pad039,Fillet011,Sketch137,Pocket034,Fillet012]
  Origin = -> Origin010
  Placement = pos=(79.6,-15.1,13.4) rot=(0,0,1;0rad)
  Tip = -> Fillet012
FEATURE [Sketcher::SketchObject] Sketch138
  ArcFitTolerance = 0
  AttachmentSupport = -> [XY_Plane011]
  FullyConstrained = false
  MakeInternals = false
  MapMode = 5
  sketch-geometry (10):
    g0: ArcOfCircle CenterX=129.871 CenterY=18.109 CenterZ=0 NormalX=0 NormalY=0 NormalZ=1 AngleXU=0 Radius=1.28321 StartAngle=1.5708 EndAngle=3.14159
    g1: LineSegment StartX=129.871 StartY=19.3922 StartZ=0 EndX=132.438 EndY=19.3922 EndZ=0
    g2: ArcOfCircle CenterX=132.438 CenterY=18.109 CenterZ=0 NormalX=0 NormalY=0 NormalZ=1 AngleXU=0 Radius=1.28321 StartAngle=1e-16 EndAngle=1.5708
    g3: LineSegment StartX=133.721 StartY=18.109 StartZ=0 EndX=133.721 EndY=12.1018 EndZ=0
    g4: ArcOfCircle CenterX=132.438 CenterY=12.1018 CenterZ=0 NormalX=0 NormalY=0 NormalZ=1 AngleXU=0 Radius=1.28321 StartAngle=4.71239 EndAngle=6.28319
    g5: LineSegment StartX=132.438 StartY=10.8186 StartZ=0 EndX=129.871 EndY=10.8186 EndZ=0
    g6: ArcOfCircle CenterX=129.871 CenterY=12.1018 CenterZ=0 NormalX=0 NormalY=0 NormalZ=1 AngleXU=0 Radius=1.28321 StartAngle=3.14159 EndAngle=4.71239
    g7: LineSegment StartX=128.588 StartY=12.1018 StartZ=0 EndX=128.588 EndY=18.109 EndZ=0
    g8: GeomPoint [constr] X=128.588 Y=19.3922 Z=0
    g9: GeomPoint [constr] X=133.721 Y=10.8186 Z=0
  constraints (19):
    c: Tangent(g0,g1) = 1.5708
    c: Tangent(g1,g2) = 1.5708
    c: Tangent(g2,g3) = 1.5708
    c: Tangent(g3,g4) = 1.5708
    c: Tangent(g4,g5) = 1.5708
    c: Tangent(g5,g6) = 1.5708
    c: Tangent(g6,g7) = 1.5708
    c: Tangent(g7,g0) = 1.5708
    c: Horizontal(g1)
    c: Horizontal(g5)
    c: Vertical(g3)
    c: Vertical(g7)
    c: Equal(g0,g2)
    c: Equal(g2,g4)
    c: Equal(g4,g6)
    c: PointOnObject(g8,g1)
    c: PointOnObject(g8,g7)
    c: PointOnObject(g9,g3)
    c: PointOnObject(g9,g5)
FEATURE [PartDesign::Pad] Pad040
  Direction = (0,0,1)
  Length = 2.5
  Length2 = 10
  Profile = -> Sketch138
  ReferenceAxis = -> Sketch138 [N_Axis]
  Suppressed = false
  Type = 0
FEATURE [Sketcher::SketchObject] Sketch139
  ArcFitTolerance = 0
  AttachmentSupport = -> [XY_Plane011]
  FullyConstrained = false
  MakeInternals = false
  MapMode = 5
  sketch-geometry (8):
    g0: LineSegment StartX=131.673 StartY=19.9314 StartZ=0 EndX=126.887 EndY=19.9314 EndZ=0
    g1: LineSegment StartX=126.173 StartY=19.2175 StartZ=0 EndX=126.173 EndY=10.9892 EndZ=0
    g2: LineSegment StartX=126.828 StartY=10.3345 StartZ=0 EndX=131.742 EndY=10.3345 EndZ=0
    g3: LineSegment StartX=132.346 StartY=10.939 StartZ=0 EndX=132.346 EndY=19.2579 EndZ=0
    g4: ArcOfCircle CenterX=126.887 CenterY=19.2175 CenterZ=0 NormalX=0 NormalY=0 NormalZ=1 AngleXU=0 Radius=0.713951 StartAngle=1.5708 EndAngle=3.14159
    g5: ArcOfCircle CenterX=126.828 CenterY=10.9892 CenterZ=0 NormalX=0 NormalY=0 NormalZ=1 AngleXU=0 Radius=0.654684 StartAngle=3.14159 EndAngle=4.71239
    g6: ArcOfCircle CenterX=131.742 CenterY=10.939 CenterZ=0 NormalX=0 NormalY=0 NormalZ=1 AngleXU=0 Radius=0.60449 StartAngle=4.71239 EndAngle=6.28319
    g7: ArcOfCircle CenterX=131.673 CenterY=19.2579 CenterZ=0 NormalX=0 NormalY=0 NormalZ=1 AngleXU=0 Radius=0.673523 StartAngle=0 EndAngle=1.5708
  constraints (12):
    c: Horizontal(g0)
    c: Horizontal(g2)
    c: Vertical(g1)
    c: Vertical(g3)
    c: Tangent(g0,g4) = -1.5708
    c: Tangent(g1,g4) = -1.5708
    c: Tangent(g1,g5) = -1.5708
    c: Tangent(g2,g5) = -1.5708
    c: Tangent(g3,g6) = -1.5708
    c: Tangent(g2,g6) = -1.5708
    c: Tangent(g0,g7) = -1.5708
    c: Tangent(g3,g7) = -1.5708
FEATURE [PartDesign::Pad] Pad041
  BaseFeature = -> Pad040
  Direction = (0,0,1)
  Length = 0.3
  Length2 = 10
  Profile = -> Sketch139
  ReferenceAxis = -> Sketch139 [N_Axis]
  Suppressed = false
  Type = 0
FEATURE [PartDesign::Fillet] Fillet014
  Base = -> Pad041 [Edge53]
  BaseFeature = -> Pad041
  Radius = 1
  SupportTransform = false
  Suppressed = false
  UseAllEdges = false
FEATURE [PartDesign::Body] Body011  label="BotonReset"
  AllowCompound = false
  Group = -> [Sketch138,Pad040,Sketch139,Pad041,Fillet014]
  Origin = -> Origin011
  Placement = pos=(0,0,20) rot=(0,0,1;0rad)
  Tip = -> Fillet014
FEATURE [PartDesign::Fillet] Fillet009
  Base = -> Pocket029 [Edge209,Edge211,Edge207,Edge208,Edge210]
  BaseFeature = -> Pocket029
  Placement = pos=(0,0,8) rot=(0,0,1;0rad)
  Radius = 2
  SupportTransform = false
  Suppressed = false
  UseAllEdges = false
FEATURE [PartDesign::Pocket] Pocket030
  BaseFeature = -> Fillet009
  Direction = (0,0,1)
  Length = 0.44
  Length2 = 5
  Placement = pos=(0,0,8) rot=(0,0,1;0rad)
  Profile = -> Sketch125
  ReferenceAxis = -> Sketch125 [N_Axis]
  Suppressed = false
  Type = 0
FEATURE [PartDesign::Fillet] Fillet013
  Base = -> Pocket030 [Edge125,Edge155,Edge159,Edge157,Edge153]
  BaseFeature = -> Pocket030
  Placement = pos=(0,0,8) rot=(0,0,1;0rad)
  Radius = 1.5
  SupportTransform = false
  Suppressed = false
  UseAllEdges = false
FEATURE [PartDesign::Fillet] Fillet015
  Base = -> Fillet013 [Edge237,Edge234,Edge233,Edge230,Edge232]
  BaseFeature = -> Fillet013
  Placement = pos=(0,0,8) rot=(0,0,1;0rad)
  Radius = 1.2
  SupportTransform = false
  Suppressed = false
  UseAllEdges = false
FEATURE [PartDesign::Body] Body007  label="Bottom"
  AllowCompound = false
  Group = -> [Sketch058,Sketch108,Pad,Pocket,Sketch118,Sketch119,Pad030,Pocket028,Sketch120,Pad031,Sketch121,Pocket029,Fillet009,Sketch125,Pocket030,Fillet013,Fillet015]
  Origin = -> Origin007
  Placement = pos=(0,0,-3) rot=(0,0,1;0rad)
  Tip = -> Fillet015
FEATURE [Sketcher::SketchObject] Sketch141
  ArcFitTolerance = 0
  FullyConstrained = false
  MakeInternals = false
  MapMode = 5
  Placement = pos=(0,0,21) rot=(0,0,1;0rad)
  sketch-geometry (8):
    g0: LineSegment StartX=118.05 StartY=60 StartZ=0 EndX=118.05 EndY=55.6867 EndZ=0
    g1: LineSegment StartX=129.65 StartY=60 StartZ=0 EndX=118.05 EndY=60 EndZ=0
    g2: LineSegment [constr] StartX=123.654 StartY=60 StartZ=0 EndX=123.654 EndY=55 EndZ=0
    g3: ArcOfCircle CenterX=119.05 CenterY=55.6867 CenterZ=0 NormalX=0 NormalY=0 NormalZ=1 AngleXU=0 Radius=1 StartAngle=3.14159 EndAngle=4.71239
    g4: LineSegment [constr] StartX=118.05 StartY=57.129 StartZ=0 EndX=129.65 EndY=57.129 EndZ=0
    g5: LineSegment StartX=119.05 StartY=54.6867 StartZ=0 EndX=128.65 EndY=54.6867 EndZ=0
    g6: LineSegment StartX=129.65 StartY=55.6867 StartZ=0 EndX=129.65 EndY=60 EndZ=0
    g7: ArcOfCircle CenterX=128.65 CenterY=55.6867 CenterZ=0 NormalX=0 NormalY=0 NormalZ=1 AngleXU=0 Radius=1 StartAngle=4.71239 EndAngle=6.28319
  constraints (18):
    c: Vertical(g0)
    c: Coincident(g1,g0)
    c: PointOnObject(g2,g1)
    c: Vertical(g2)
    c: Distance(g2) = 5
    c: Tangent(g0,g3) = -1.5708
    c: Radius(g3) = 1
    c: PointOnObject(g4,g0)
    c: Horizontal(g4)
    c: Distance(g4) = 11.6
    c: Coincident(g5,g3)
    c: Horizontal(g5)
    c: Vertical(g6)
    c: Coincident(g1,g6)
    c: Tangent(g6,g7) = -1.5708
    c: Tangent(g5,g7) = -1.5708
    c: Radius(g7) = 1
    c: PointOnObject(g4,g6)
FEATURE [PartDesign::Pocket] Pocket035  label="USBC Top Hole"
  BaseFeature = -> Pocket031
  Direction = (0,0,-1)
  Length = 5
  Length2 = 5
  Placement = pos=(0,0,8) rot=(0,0,1;0rad)
  Profile = -> Sketch141
  ReferenceAxis = -> Sketch141 [N_Axis]
  Suppressed = false
  Type = 0
FEATURE [Sketcher::SketchObject] Sketch142
  ArcFitTolerance = 0
  AttachmentSupport = -> [Pocket035]
  ExternalGeometry = -> [Sketch126]
  FullyConstrained = false
  MakeInternals = false
  MapMode = 5
  Placement = pos=(0,0,16.5) rot=(1,0,0;3.14159rad)
  sketch-geometry (6):
    g0: Circle CenterX=94.55 CenterY=-41.5 CenterZ=0 NormalX=0 NormalY=0 NormalZ=1 AngleXU=0 Radius=2
    g1: Circle CenterX=18.6 CenterY=-18.76 CenterZ=0 NormalX=0 NormalY=0 NormalZ=1 AngleXU=0 Radius=2
    g2: Circle CenterX=18.61 CenterY=-37.51 CenterZ=0 NormalX=0 NormalY=0 NormalZ=1 AngleXU=0 Radius=2
    g3: Circle CenterX=61.84 CenterY=-1.51 CenterZ=0 NormalX=0 NormalY=0 NormalZ=1 AngleXU=0 Radius=2
    g4: Circle CenterX=108.3 CenterY=6.24 CenterZ=0 NormalX=0 NormalY=0 NormalZ=1 AngleXU=0 Radius=1.7
    g5: Circle CenterX=108.3 CenterY=6.24 CenterZ=0 NormalX=0 NormalY=0 NormalZ=1 AngleXU=0 Radius=2
  constraints (9):
    c: Radius(g0) = 2
    c: Coincident(g1,g-4)
    c: Radius(g1) = 2
    c: Coincident(g2,g-3)
    c: Radius(g2) = 2
    c: Coincident(g3,g-5)
    c: Radius(g3) = 2
    c: Coincident(g5,g4)
    c: Radius(g5) = 2
FEATURE [PartDesign::Pocket] Pocket036  label="Threaded Insert Hole"
  BaseFeature = -> Pocket035
  Direction = (0,0,1)
  Length = 1
  Length2 = 5
  Placement = pos=(0,0,8) rot=(0,0,1;0rad)
  Profile = -> Sketch142
  ReferenceAxis = -> Sketch142 [N_Axis]
  Suppressed = false
  Type = 0
FEATURE [PartDesign::Body] Body008  label="Top"
  AllowCompound = false
  Group = -> [Sketch109,Sketch110,Pad028,Pocket021,Fillet003,Sketch111,Pocket022,Sketch114,Pocket023,Sketch115,Pocket024,Sketch116,Pocket025,Sketch,Pocket026,Fillet,Fillet006,Sketch079,Pad032,Sketch126,Pocket031,Sketch141,Pocket035,Sketch142,Pocket036]
  Origin = -> Origin008
  Tip = -> Pocket036
FEATURE [Sketcher::SketchObject] Sketch143
  ArcFitTolerance = 0
  FullyConstrained = false
  MakeInternals = false
  Placement = pos=(0,0,8) rot=(0,0,1;0rad)
  sketch-geometry (26):
    g0: LineSegment StartX=-0.575516 StartY=59.75 StartZ=0 EndX=34.48 EndY=59.75 EndZ=0
    g1: LineSegment StartX=34.48 StartY=59.75 StartZ=0 EndX=34.48 EndY=61.4175 EndZ=0
    g2: ArcOfCircle CenterX=37.5625 CenterY=61.4175 CenterZ=0 NormalX=0 NormalY=0 NormalZ=1 AngleXU=0 Radius=3.08246 StartAngle=1.5708 EndAngle=3.14159
    g3: LineSegment StartX=37.5625 StartY=64.5 StartZ=0 EndX=53.5746 EndY=64.5 EndZ=0
    g4: ArcOfCircle CenterX=56.4769 CenterY=63.7531 CenterZ=0 NormalX=0 NormalY=0 NormalZ=1 AngleXU=0 Radius=2.99694 StartAngle=1.5708 EndAngle=2.8897
    g5: LineSegment StartX=56.4769 StartY=66.75 StartZ=0 EndX=75.4511 EndY=66.75 EndZ=0
    g6: ArcOfCircle CenterX=75.4511 CenterY=63.7211 CenterZ=0 NormalX=0 NormalY=0 NormalZ=1 AngleXU=0 Radius=3.0289 StartAngle=0.260077 EndAngle=1.5708
    g7: LineSegment StartX=78.3781 StartY=64.5 StartZ=0 EndX=94.3924 EndY=64.5 EndZ=0
    g8: ArcOfCircle CenterX=94.3924 CenterY=61.4124 CenterZ=0 NormalX=0 NormalY=0 NormalZ=1 AngleXU=0 Radius=3.08765 StartAngle=0.274732 EndAngle=1.5708
    g9: LineSegment StartX=97.3642 StartY=62.25 StartZ=0 EndX=113.447 EndY=62.25 EndZ=0
    g10: ArcOfCircle CenterX=113.447 CenterY=59.2166 CenterZ=0 NormalX=0 NormalY=0 NormalZ=1 AngleXU=0 Radius=3.03342 StartAngle=0.261223 EndAngle=1.5708
    g11: LineSegment StartX=116.377 StartY=60 StartZ=0 EndX=134.174 EndY=60 EndZ=0
    g12: ArcOfCircle CenterX=134.174 CenterY=56.9441 CenterZ=0 NormalX=0 NormalY=0 NormalZ=1 AngleXU=0 Radius=3.05595 StartAngle=0 EndAngle=1.5708
    g13: LineSegment StartX=137.23 StartY=56.9441 StartZ=0 EndX=137.23 EndY=-3.79962 EndZ=0
    g14: ArcOfCircle CenterX=132.762 CenterY=-3.79962 CenterZ=0 NormalX=0 NormalY=0 NormalZ=1 AngleXU=0 Radius=4.46789 StartAngle=5.76566 EndAngle=6.28319
    g15: LineSegment StartX=136.645 StartY=-6.01003 StartZ=0 EndX=122.927 EndY=-30.1062 EndZ=0
    g16: ArcOfCircle CenterX=119.558 CenterY=-28.1883 CenterZ=0 NormalX=0 NormalY=0 NormalZ=1 AngleXU=0 Radius=3.87659 StartAngle=4.18792 EndAngle=5.76566
    g17: LineSegment StartX=117.617 StartY=-31.5438 StartZ=0 EndX=103.226 EndY=-23.2181 EndZ=0
    g18: ArcOfCircle CenterX=102.379 CenterY=-24.6817 CenterZ=0 NormalX=0 NormalY=0 NormalZ=1 AngleXU=0 Radius=1.69085 StartAngle=1.04632 EndAngle=1.44147
    g19: LineSegment StartX=102.597 StartY=-23.0049 StartZ=0 EndX=66.2389 EndY=-18.2764 EndZ=0
    g20: ArcOfCircle CenterX=66.7544 CenterY=-14.3127 CenterZ=0 NormalX=0 NormalY=0 NormalZ=1 AngleXU=0 Radius=3.99704 StartAngle=3.77183 EndAngle=4.58306
    g21: LineSegment StartX=63.5253 StartY=-16.6683 StartZ=0 EndX=53.9192 EndY=-3.5 EndZ=0
    g22: LineSegment StartX=53.9192 StartY=-3.5 StartZ=0 EndX=-0.150389 EndY=-3.5 EndZ=0
    g23: ArcOfCircle CenterX=-0.150389 CenterY=-0.150389 CenterZ=0 NormalX=0 NormalY=0 NormalZ=1 AngleXU=0 Radius=3.34961 StartAngle=3.14159 EndAngle=4.71239
    g24: LineSegment StartX=-3.5 StartY=-0.150389 StartZ=0 EndX=-3.5 EndY=56.8255 EndZ=0
    g25: ArcOfCircle CenterX=-0.575516 CenterY=56.8255 CenterZ=0 NormalX=0 NormalY=0 NormalZ=1 AngleXU=0 Radius=2.92448 StartAngle=1.5708 EndAngle=3.14159
  constraints (36):
    c: Horizontal(g0)
    c: Coincident(g0,g1)
    c: Vertical(g1)
    c: Coincident(g1,g2)
    c: Coincident(g2,g3)
    c: Horizontal(g3)
    c: Coincident(g3,g4)
    c: Coincident(g4,g5)
    c: Horizontal(g5)
    c: Coincident(g5,g6)
    c: Coincident(g6,g7)
    c: Horizontal(g7)
    c: Coincident(g7,g8)
    c: Coincident(g8,g9)
    c: Horizontal(g9)
    c: Coincident(g9,g10)
    c: Coincident(g10,g11)
    c: Horizontal(g11)
    c: Coincident(g11,g12)
    c: Coincident(g12,g13)
    c: Vertical(g13)
    c: Coincident(g13,g14)
    c: Coincident(g14,g15)
    c: Coincident(g15,g16)
    c: Coincident(g16,g17)
    c: Coincident(g17,g18)
    c: Coincident(g18,g19)
    c: Coincident(g19,g20)
    c: Coincident(g20,g21)
    c: Coincident(g21,g22)
    c: Horizontal(g22)
    c: Coincident(g22,g23)
    c: Coincident(g23,g24)
    c: Vertical(g24)
    c: Coincident(g24,g25)
    c: Coincident(g25,g0)
